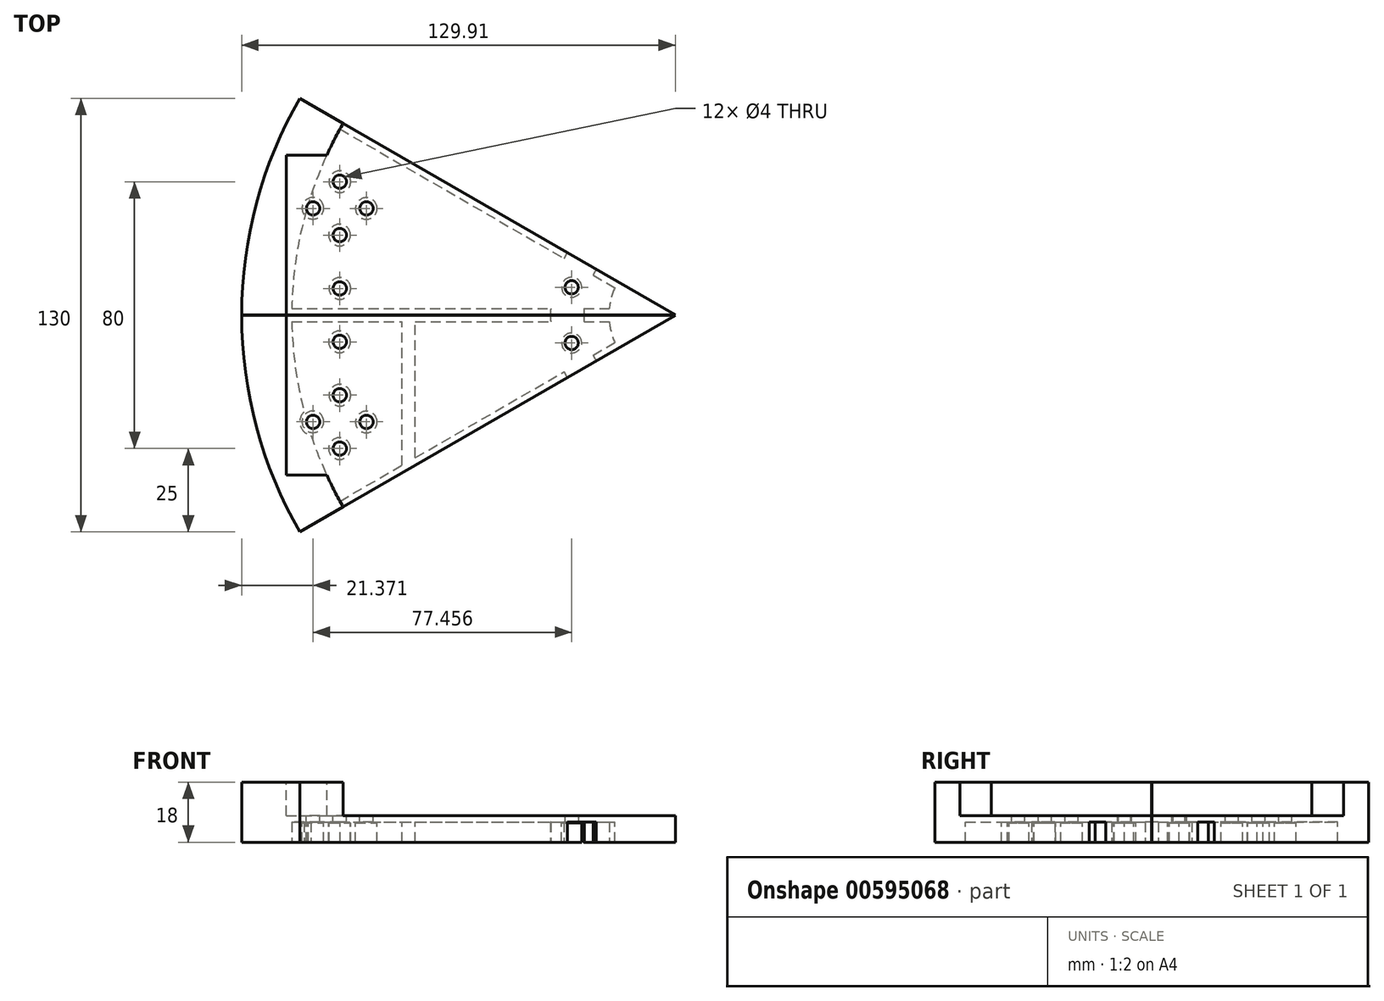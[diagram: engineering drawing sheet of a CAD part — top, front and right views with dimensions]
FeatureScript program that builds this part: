
annotation { "Feature Type Name" : "Feature", "Feature Type Description" : "" }
export const myFeature = defineFeature(function(context is Context, id is Id, definition is map)
    precondition{}
    {
        {
            var Q0;
            Q0=qCreatedBy(makeId("Front.planeOp"),FACE);
            var sketch = newSketch(context, id + "F0", { "sketchPlane" : qUnion([Q0])});
            skLineSegment(sketch, "E0.bottom", {"start": v(-45.23, 10.4) * mm, "end": v(-30.23, 10.4) * mm});
            skLineSegment(sketch, "E0.top", {"start": v(-45.23, -7.6) * mm, "end": v(-30.23, -7.6) * mm});
            skLineSegment(sketch, "E0.left", {"start": v(-45.23, 10.4) * mm, "end": v(-45.23, -7.6) * mm});
            skLineSegment(sketch, "E0.right", {"start": v(-30.23, 10.4) * mm, "end": v(-30.23, -7.6) * mm});
            skLineSegment(sketch, "E1.bottom", {"start": v(-30.23, -1.6) * mm, "end": v(84.77, -1.6) * mm});
            skLineSegment(sketch, "E1.top", {"start": v(-30.23, 0.4) * mm, "end": v(84.77, 0.4) * mm});
            skLineSegment(sketch, "E1.left", {"start": v(-30.23, -1.6) * mm, "end": v(-30.23, 0.4) * mm});
            skLineSegment(sketch, "E1.right", {"start": v(84.77, -1.6) * mm, "end": v(84.77, 0.4) * mm});
            skLineSegment(sketch, "E2.bottom", {"start": v(84.77, 0.4) * mm, "end": v(64.77, 0.4) * mm});
            skLineSegment(sketch, "E2.top", {"start": v(84.77, -7.6) * mm, "end": v(64.77, -7.6) * mm});
            skLineSegment(sketch, "E2.left", {"start": v(84.77, 0.4) * mm, "end": v(84.77, -7.6) * mm});
            skLineSegment(sketch, "E2.right", {"start": v(64.77, 0.4) * mm, "end": v(64.77, -7.6) * mm});
            skSolve(sketch);
        }
        {
            var Q0;
            {var subQ1=sQuery(id+"F0.wireOp",EDGE,"E0.bottom");Q0=makeQuery(id+"F0.imprint","IMPRINT",FACE,{"disambiguationData":[TD([[makeQuery(id+"F0.imprint","IMPRINT",EDGE,{"derivedFrom":subQ1}),-1.0]])]});}
            var Q1;
            {var subQ5=sQuery(id+"F0.wireOp",EDGE,"E2.top");Q1=makeQuery(id+"F0.imprint","IMPRINT",FACE,{"disambiguationData":[TD([[makeQuery(id+"F0.imprint","IMPRINT",EDGE,{"derivedFrom":subQ5}),-1.0]])]});}
            var Q2;
            {var subQ4=sQuery(id+"F0.wireOp",EDGE,"E1.top");Q2=makeQuery(id+"F0.imprint","IMPRINT",FACE,{"disambiguationData":[TD([[makeQuery(id+"F0.imprint","IMPRINT",EDGE,{"derivedFrom":subQ4}),-1.0]])]});}
            var Q3;
            {var subQ5=sQuery(id+"F0.wireOp",EDGE,"E2.bottom");Q3=makeQuery(id+"F0.imprint","IMPRINT",FACE,{"disambiguationData":[TD([[makeQuery(id+"F0.imprint","IMPRINT",EDGE,{"derivedFrom":subQ5}),1.0]])]});}
            var Q4;
            Q4=sQuery(id+"F0.wireOp",EDGE,"E1.right");
            revolve(context, id + "F1", {"entities" : qUnion([Q0, Q1, Q2, Q3]), "axis" : qUnion([Q4]), "revolveType" : RevolveType.SYMMETRIC, "angle" : 60 * degree});
        }
        {
            var Q0;
            Q0=makeQuery(id+"F1.opRevolve","SWEPT_FACE",FACE,{"disambiguationData":[OSD([sQuery(id+"F0.wireOp",EDGE,"E0.bottom")])]});
            var sketch = newSketch(context, id + "F2", { "sketchPlane" : qUnion([Q0])});
            skLineSegment(sketch, "E3.bottom", {"start": v(-31.86, 48) * mm, "end": v(0.14, 48) * mm});
            skLineSegment(sketch, "E3.top", {"start": v(-31.86, -48) * mm, "end": v(0.14, -48) * mm});
            skLineSegment(sketch, "E3.left", {"start": v(-31.86, 48) * mm, "end": v(-31.86, -48) * mm});
            skLineSegment(sketch, "E3.right", {"start": v(0.14, 48) * mm, "end": v(0.14, -48) * mm});
            skLineSegment(sketch, "E4", {"start": v(12.42, 124.7) * mm, "end": v(-58.42, 2) * mm});
            skSolve(sketch);
        }
        {
            var Q0;
            {var subQ0=sQuery(id+"F0.wireOp",EDGE,"E1.bottom");Q0=makeQuery(id+"F8.boolean.opBoolean","MERGE",FACE,{"derivedFrom":[makeQuery(id+"F1.opRevolve","SWEPT_FACE",FACE,{"disambiguationData":[OSD([subQ0])]}),makeQuery(id+"F8.opExtrude","CAP_FACE",FACE,{"disambiguationData":[OSD([subQ0]),OD(0.0)],"isStart":false}),makeQuery(id+"F8.opExtrude","CAP_FACE",FACE,{"disambiguationData":[OSD([subQ0]),OD(1.0)],"isStart":false})]});}
            var sketch = newSketch(context, id + "F3", { "sketchPlane" : qUnion([Q0])});
            skLineSegment(sketch, "E5.bottom", {"start": v(-42.98, 2) * mm, "end": v(77.02, 2) * mm});
            skLineSegment(sketch, "E5.top", {"start": v(-42.98, -2) * mm, "end": v(77.02, -2) * mm});
            skLineSegment(sketch, "E5.left", {"start": v(-42.98, 2) * mm, "end": v(-42.98, -2) * mm});
            skLineSegment(sketch, "E5.right", {"start": v(77.02, 2) * mm, "end": v(77.02, -2) * mm});
            skLineSegment(sketch, "E6.1.0", {"start": v(-26.87, -62.14) * mm, "end": v(77.06, -2.14) * mm});
            skLineSegment(sketch, "E6.1.1", {"start": v(-24.87, -65.6) * mm, "end": v(79.06, -5.6) * mm});
            skLineSegment(sketch, "E6.1.2", {"start": v(77.06, -2.14) * mm, "end": v(79.06, -5.6) * mm});
            skLineSegment(sketch, "E6.1.3", {"start": v(-26.87, -62.14) * mm, "end": v(-24.87, -65.6) * mm});
            skLineSegment(sketch, "E6.2.2", {"start": v(79.16, -5.71) * mm, "end": v(82.62, -7.71) * mm});
            skLineSegment(sketch, "E6.3.2", {"start": v(82.77, -7.75) * mm, "end": v(86.77, -7.75) * mm});
            skLineSegment(sketch, "E6.4.2", {"start": v(86.9, -7.71) * mm, "end": v(90.37, -5.71) * mm});
            skLineSegment(sketch, "E6.5.2", {"start": v(90.48, -5.6) * mm, "end": v(92.48, -2.14) * mm});
            skLineSegment(sketch, "E6.6.2", {"start": v(92.51, -2) * mm, "end": v(92.51, 2) * mm});
            skLineSegment(sketch, "E6.7.2", {"start": v(92.48, 2.14) * mm, "end": v(90.48, 5.6) * mm});
            skLineSegment(sketch, "E6.8.2", {"start": v(90.37, 5.71) * mm, "end": v(86.9, 7.71) * mm});
            skLineSegment(sketch, "E6.9.2", {"start": v(86.77, 7.75) * mm, "end": v(82.77, 7.75) * mm});
            skLineSegment(sketch, "E6.10.2", {"start": v(82.62, 7.71) * mm, "end": v(79.16, 5.71) * mm});
            skLineSegment(sketch, "E6.11.0", {"start": v(-24.87, 65.6) * mm, "end": v(79.06, 5.6) * mm});
            skLineSegment(sketch, "E6.11.1", {"start": v(-26.87, 62.14) * mm, "end": v(77.06, 2.14) * mm});
            skLineSegment(sketch, "E6.11.2", {"start": v(79.06, 5.6) * mm, "end": v(77.06, 2.14) * mm});
            skLineSegment(sketch, "E6.11.3", {"start": v(-24.87, 65.6) * mm, "end": v(-26.87, 62.14) * mm});
            skPoint(sketch, "E6.center", {"position": v(84.77, 0) * mm});
            skSolve(sketch);
        }
        {
            var Q0;
            {var subQ2=sQuery(id+"F0.wireOp",EDGE,"E1.bottom");var subQ10=makeQuery(id+"F1.opRevolve","CAP_EDGE",EDGE,{"disambiguationData":[OSD([subQ2])],"isStart":false});Q0=makeQuery(id+"F3.imprint","IMPRINT",FACE,{"disambiguationData":[TD([[makeQuery(id+"F3.imprint","IMPRINT",EDGE,{"derivedFrom":subQ10}),-1.0]])]});}
            var Q1;
            {var subQ0=sQuery(id+"F3.wireOp",EDGE,"E5.bottom");var subQ1=sQuery(id+"F0.wireOp",EDGE,"E1.bottom");var subQ2=makeQuery(id+"F1.opRevolve","SWEPT_EDGE",EDGE,{"disambiguationData":[OSD([subQ1,sQuery(id+"F0.wireOp",EDGE,"E2.right")])]});var subQ3=makeQuery(id+"F3.imprint","INTERSECT",VERTEX,{"derivedFrom":[subQ2,subQ0]});Q1=makeQuery(id+"F3.imprint","IMPRINT",FACE,{"disambiguationData":[TD([[makeQuery(id+"F3.imprint","IMPRINT",EDGE,{"disambiguationData":[TD([[subQ3,1.0]])],"derivedFrom":subQ0}),-1.0]])]});}
            var Q2;
            {var subQ2=sQuery(id+"F0.wireOp",EDGE,"E1.bottom");var subQ10=makeQuery(id+"F1.opRevolve","CAP_EDGE",EDGE,{"disambiguationData":[OSD([subQ2])],"isStart":true});Q2=makeQuery(id+"F3.imprint","IMPRINT",FACE,{"disambiguationData":[TD([[makeQuery(id+"F3.imprint","IMPRINT",EDGE,{"derivedFrom":subQ10}),1.0]])]});}
            var Q3;
            {var subQ0=sQuery(id+"F3.wireOp",EDGE,"E5.bottom");var subQ3=sQuery(id+"F0.wireOp",EDGE,"E1.bottom");var subQ4=makeQuery(id+"F1.opRevolve","SWEPT_FACE",FACE,{"disambiguationData":[OSD([subQ3])]});var subQ7=makeQuery(id+"F9.boolean.opBoolean","INTERSECT",EDGE,{"derivedFrom":[subQ4,makeQuery(id+"F9.opExtrude","SWEPT_FACE",FACE,{"disambiguationData":[OSD([sQuery(id+"F7.wireOp",EDGE,"E14.0.1.6")])]})]});var subQ8=makeQuery(id+"F3.imprint","INTERSECT",VERTEX,{"derivedFrom":[subQ7,subQ0]});Q3=makeQuery(id+"F3.imprint","IMPRINT",FACE,{"disambiguationData":[TD([[makeQuery(id+"F3.imprint","IMPRINT",EDGE,{"disambiguationData":[TD([[subQ8,1.0]])],"derivedFrom":subQ7}),1.0]])]});}
            var Q4;
            {var subQ0=sQuery(id+"F3.wireOp",EDGE,"E5.bottom");var subQ1=makeQuery(id+"F1.opRevolve","SWEPT_FACE",FACE,{"disambiguationData":[OSD([sQuery(id+"F0.wireOp",EDGE,"E1.bottom")])]});var subQ2=makeQuery(id+"F9.boolean.opBoolean","INTERSECT",EDGE,{"derivedFrom":[subQ1,makeQuery(id+"F9.opExtrude","SWEPT_FACE",FACE,{"disambiguationData":[OSD([sQuery(id+"F7.wireOp",EDGE,"E14.0.1.6")])]})]});var subQ3=makeQuery(id+"F3.imprint","INTERSECT",VERTEX,{"derivedFrom":[subQ2,subQ0]});Q4=makeQuery(id+"F3.imprint","IMPRINT",FACE,{"disambiguationData":[TD([[makeQuery(id+"F3.imprint","IMPRINT",EDGE,{"disambiguationData":[TD([[subQ3,-1.0]])],"derivedFrom":subQ0}),-1.0]])]});}
            extrude(context, id + "F4", {"entities" : qUnion([Q0, Q1, Q2, Q3, Q4]), "operationType" : NewBodyOperationType.ADD, "depth" : 6 * mm, "offsetDistance" : 25 * mm});
        }
        {
            var Q0;
            {var subQ0=sQuery(id+"F2.wireOp",EDGE,"E3.left");Q0=makeQuery(id+"F2.imprint","IMPRINT",FACE,{"disambiguationData":[TD([[makeQuery(id+"F2.imprint","IMPRINT",EDGE,{"derivedFrom":subQ0}),1.0]])]});}
            extrude(context, id + "F5", {"entities" : qUnion([Q0]), "operationType" : NewBodyOperationType.REMOVE, "oppositeDirection" : true, "depth" : 10 * mm, "offsetDistance" : 25 * mm});
        }
        {
            var Q0;
            {var subQ0=sQuery(id+"F0.wireOp",EDGE,"E2.right");var subQ1=sQuery(id+"F0.wireOp",EDGE,"E1.left");var subQ2=sQuery(id+"F0.wireOp",EDGE,"E1.bottom");var subQ3=sQuery(id+"F0.wireOp",EDGE,"E0.right");Q0=makeQuery(id+"F4.boolean.opBoolean","MERGE",FACE,{"derivedFrom":[makeQuery(id+"F1.opRevolve","SWEPT_FACE",FACE,{"disambiguationData":[OSD([sQuery(id+"F0.wireOp",EDGE,"E0.top")])]}),makeQuery(id+"F1.opRevolve","SWEPT_FACE",FACE,{"disambiguationData":[OSD([sQuery(id+"F0.wireOp",EDGE,"E2.top")])]}),makeQuery(id+"F4.opExtrude","CAP_FACE",FACE,{"disambiguationData":[OSD([sQuery(id+"F3.wireOp",EDGE,"E5.bottom"),sQuery(id+"F3.wireOp",EDGE,"E5.top"),sQuery(id+"F3.wireOp",EDGE,"E5.left"),sQuery(id+"F3.wireOp",EDGE,"E5.right")])],"isStart":false}),makeQuery(id+"F4.opExtrude","CAP_FACE",FACE,{"disambiguationData":[OSD([subQ3,subQ2,subQ1,subQ0,sQuery(id+"F3.wireOp",EDGE,"E6.1.0")])],"isStart":false}),makeQuery(id+"F4.opExtrude","CAP_FACE",FACE,{"disambiguationData":[OSD([subQ3,subQ2,subQ1,subQ0,sQuery(id+"F3.wireOp",EDGE,"E6.11.1")])],"isStart":false})]});}
            var sketch = newSketch(context, id + "F6", { "sketchPlane" : qUnion([Q0])});
            skCircle(sketch, "E7", {"center": v(-23.86, 32) * mm, "radius": 4 * mm});
            skCircle(sketch, "E8", {"center": v(-23.86, -32) * mm, "radius": 4 * mm});
            skCircle(sketch, "E9", {"center": v(-23.84, 0) * mm, "radius": 4 * mm});
            skCircle(sketch, "E10", {"center": v(-7.64, 0) * mm, "radius": 4 * mm});
            skSolve(sketch);
        }
        {
            var Q0;
            Q0=makeQuery(id+"F5.boolean.opBoolean","MERGE",FACE,{"derivedFrom":[makeQuery(id+"F1.opRevolve","SWEPT_FACE",FACE,{"disambiguationData":[OSD([sQuery(id+"F0.wireOp",EDGE,"E1.top"),sQuery(id+"F0.wireOp",EDGE,"E2.bottom")])]}),makeQuery(id+"F5.opExtrude","CAP_FACE",FACE,{"disambiguationData":[OSD([sQuery(id+"F0.wireOp",EDGE,"E0.bottom"),sQuery(id+"F0.wireOp",EDGE,"E0.right"),sQuery(id+"F2.wireOp",EDGE,"E3.bottom"),sQuery(id+"F2.wireOp",EDGE,"E3.top"),sQuery(id+"F2.wireOp",EDGE,"E3.left")])],"isStart":false})]});
            var sketch = newSketch(context, id + "F7", { "sketchPlane" : qUnion([Q0])});
            skCircle(sketch, "E11", {"center": v(-15.86, 32) * mm, "radius": 8 * mm});
            skCircle(sketch, "E12", {"center": v(-15.86, 40) * mm, "radius": 2 * mm});
            skCircle(sketch, "E13.1.0", {"center": v(-21.52, 37.66) * mm, "radius": 2 * mm});
            skCircle(sketch, "E13.2.0", {"center": v(-23.86, 32) * mm, "radius": 2 * mm});
            skCircle(sketch, "E13.3.0", {"center": v(-21.52, 26.34) * mm, "radius": 2 * mm});
            skCircle(sketch, "E13.4.0", {"center": v(-15.86, 24) * mm, "radius": 2 * mm});
            skCircle(sketch, "E13.5.0", {"center": v(-10.2, 26.34) * mm, "radius": 2 * mm});
            skCircle(sketch, "E13.6.0", {"center": v(-7.86, 32) * mm, "radius": 2 * mm});
            skCircle(sketch, "E13.7.0", {"center": v(-10.2, 37.66) * mm, "radius": 2 * mm});
            skCircle(sketch, "E14.0.1.0", {"center": v(-15.86, 8) * mm, "radius": 2 * mm});
            skCircle(sketch, "E14.0.1.1", {"center": v(-10.2, 5.66) * mm, "radius": 2 * mm});
            skCircle(sketch, "E14.0.1.2", {"center": v(-7.86, 0) * mm, "radius": 2 * mm});
            skCircle(sketch, "E14.0.1.3", {"center": v(-10.2, -5.66) * mm, "radius": 2 * mm});
            skCircle(sketch, "E14.0.1.4", {"center": v(-15.86, -8) * mm, "radius": 2 * mm});
            skCircle(sketch, "E14.0.1.5", {"center": v(-21.52, -5.66) * mm, "radius": 2 * mm});
            skCircle(sketch, "E14.0.1.6", {"center": v(-23.86, 0) * mm, "radius": 2 * mm});
            skCircle(sketch, "E14.0.1.7", {"center": v(-21.52, 5.66) * mm, "radius": 2 * mm});
            skCircle(sketch, "E14.0.2.0", {"center": v(-15.86, -24) * mm, "radius": 2 * mm});
            skCircle(sketch, "E14.0.2.1", {"center": v(-10.2, -26.34) * mm, "radius": 2 * mm});
            skCircle(sketch, "E14.0.2.2", {"center": v(-7.86, -32) * mm, "radius": 2 * mm});
            skCircle(sketch, "E14.0.2.3", {"center": v(-10.2, -37.66) * mm, "radius": 2 * mm});
            skCircle(sketch, "E14.0.2.4", {"center": v(-15.86, -40) * mm, "radius": 2 * mm});
            skCircle(sketch, "E14.0.2.5", {"center": v(-21.52, -37.66) * mm, "radius": 2 * mm});
            skCircle(sketch, "E14.0.2.6", {"center": v(-23.86, -32) * mm, "radius": 2 * mm});
            skCircle(sketch, "E14.0.2.7", {"center": v(-21.52, -26.34) * mm, "radius": 2 * mm});
            skLineSegment(sketch, "E14.direction1", {"start": v(-21.52, 26.34) * mm, "end": v(3.48, 26.34) * mm, "construction": true});
            skLineSegment(sketch, "E14.direction2", {"start": v(-21.52, 26.34) * mm, "end": v(-21.52, -5.66) * mm, "construction": true});
            skSolve(sketch);
        }
        {
            var Q0;
            {var subQ3=sQuery(id+"F0.wireOp",EDGE,"E0.top");var subQ5=makeQuery(id+"F1.opRevolve","SWEPT_FACE",FACE,{"disambiguationData":[OSD([subQ3])]});var subQ6=makeQuery(id+"F9.opExtrude","SWEPT_FACE",FACE,{"disambiguationData":[OSD([sQuery(id+"F7.wireOp",EDGE,"E13.2.0")])]});var subQ12=makeQuery(id+"F9.boolean.opBoolean","INTERSECT",EDGE,{"derivedFrom":[subQ5,subQ6]});Q0=makeQuery(id+"F6.imprint","IMPRINT",FACE,{"disambiguationData":[TD([[makeQuery(id+"F6.imprint","IMPRINT",EDGE,{"derivedFrom":subQ12}),1.0]])]});}
            var Q1;
            {var subQ3=sQuery(id+"F0.wireOp",EDGE,"E0.top");var subQ4=makeQuery(id+"F1.opRevolve","SWEPT_FACE",FACE,{"disambiguationData":[OSD([subQ3])]});var subQ6=makeQuery(id+"F9.opExtrude","SWEPT_FACE",FACE,{"disambiguationData":[OSD([sQuery(id+"F7.wireOp",EDGE,"E14.0.2.6")])]});var subQ12=makeQuery(id+"F9.boolean.opBoolean","INTERSECT",EDGE,{"derivedFrom":[subQ4,subQ6]});Q1=makeQuery(id+"F6.imprint","IMPRINT",FACE,{"disambiguationData":[TD([[makeQuery(id+"F6.imprint","IMPRINT",EDGE,{"derivedFrom":subQ12}),1.0]])]});}
            var Q2;
            {var subQ0=sQuery(id+"F6.wireOp",EDGE,"E9");var subQ1=makeQuery(id+"F4.opExtrude","CAP_EDGE",EDGE,{"disambiguationData":[OSD([sQuery(id+"F3.wireOp",EDGE,"E5.bottom")])],"isStart":false});var subQ2=makeQuery(id+"F6.imprint","INTERSECT",VERTEX,{"disambiguationData":[OD(0.0)],"derivedFrom":[subQ1,subQ0]});Q2=makeQuery(id+"F6.imprint","IMPRINT",FACE,{"disambiguationData":[TD([[makeQuery(id+"F6.imprint","IMPRINT",EDGE,{"disambiguationData":[TD([[subQ2,-1.0]])],"derivedFrom":subQ0}),1.0]])]});}
            var Q3;
            {var subQ0=sQuery(id+"F6.wireOp",EDGE,"E10");var subQ1=makeQuery(id+"F4.opExtrude","CAP_EDGE",EDGE,{"disambiguationData":[OSD([sQuery(id+"F3.wireOp",EDGE,"E5.bottom")])],"isStart":false});var subQ2=makeQuery(id+"F6.imprint","INTERSECT",VERTEX,{"disambiguationData":[OD(0.0)],"derivedFrom":[subQ1,subQ0]});Q3=makeQuery(id+"F6.imprint","IMPRINT",FACE,{"disambiguationData":[TD([[makeQuery(id+"F6.imprint","IMPRINT",EDGE,{"disambiguationData":[TD([[subQ2,-1.0]])],"derivedFrom":subQ0}),1.0]])]});}
            var Q4;
            {var subQ0=sQuery(id+"F6.wireOp",EDGE,"E7");var subQ1=sQuery(id+"F3.wireOp",EDGE,"E5.bottom");var subQ6=sQuery(id+"F0.wireOp",EDGE,"E0.right");var subQ7=sQuery(id+"F0.wireOp",EDGE,"E0.top");var subQ8=makeQuery(id+"F4.boolean.opBoolean","SPLIT",EDGE,{"disambiguationData":[TD([makeQuery(id+"F4.opExtrude","SWEPT_FACE",FACE,{"disambiguationData":[OSD([subQ1])]})])],"derivedFrom":makeQuery(id+"F1.opRevolve","SWEPT_EDGE",EDGE,{"disambiguationData":[OSD([subQ7,subQ6])]})});var subQ9=makeQuery(id+"F6.imprint","INTERSECT",VERTEX,{"disambiguationData":[OD(0.0)],"derivedFrom":[subQ8,subQ0]});Q4=makeQuery(id+"F6.imprint","IMPRINT",FACE,{"disambiguationData":[TD([[makeQuery(id+"F6.imprint","IMPRINT",EDGE,{"disambiguationData":[TD([[subQ9,-1.0]])],"derivedFrom":subQ0}),1.0]])]});}
            var Q5;
            {var subQ0=sQuery(id+"F6.wireOp",EDGE,"E8");var subQ1=sQuery(id+"F3.wireOp",EDGE,"E5.top");var subQ5=sQuery(id+"F0.wireOp",EDGE,"E0.right");var subQ6=sQuery(id+"F0.wireOp",EDGE,"E0.top");var subQ8=makeQuery(id+"F4.boolean.opBoolean","SPLIT",EDGE,{"disambiguationData":[TD([makeQuery(id+"F4.opExtrude","SWEPT_FACE",FACE,{"disambiguationData":[OSD([subQ1])]})])],"derivedFrom":makeQuery(id+"F1.opRevolve","SWEPT_EDGE",EDGE,{"disambiguationData":[OSD([subQ6,subQ5])]})});var subQ9=makeQuery(id+"F6.imprint","INTERSECT",VERTEX,{"disambiguationData":[OD(0.0)],"derivedFrom":[subQ8,subQ0]});Q5=makeQuery(id+"F6.imprint","IMPRINT",FACE,{"disambiguationData":[TD([[makeQuery(id+"F6.imprint","IMPRINT",EDGE,{"disambiguationData":[TD([[subQ9,1.0]])],"derivedFrom":subQ0}),1.0]])]});}
            var Q6;
            Q6=makeQuery(id+"F1.opRevolve","SWEPT_FACE",FACE,{"disambiguationData":[OSD([sQuery(id+"F0.wireOp",EDGE,"E1.bottom")])]});
            extrude(context, id + "F8", {"entities" : qUnion([Q0, Q1, Q2, Q3, Q4, Q5]), "operationType" : NewBodyOperationType.REMOVE, "endBound" : BoundingType.UP_TO_SURFACE, "oppositeDirection" : true, "depth" : 25 * mm, "endBoundEntityFace" : qUnion([Q6]), "offsetDistance" : 25 * mm});
        }
        {
            var Q0;
            Q0=makeQuery(id+"F7.imprint","IMPRINT",FACE,{"disambiguationData":[TD([[makeQuery(id+"F7.imprint","IMPRINT",EDGE,{"derivedFrom":sQuery(id+"F7.wireOp",EDGE,"E14.0.2.6")}),1.0]])]});
            var Q1;
            Q1=makeQuery(id+"F7.imprint","IMPRINT",FACE,{"disambiguationData":[TD([[makeQuery(id+"F7.imprint","IMPRINT",EDGE,{"derivedFrom":sQuery(id+"F7.wireOp",EDGE,"E14.0.2.4")}),1.0]])]});
            var Q2;
            Q2=makeQuery(id+"F7.imprint","IMPRINT",FACE,{"disambiguationData":[TD([[makeQuery(id+"F7.imprint","IMPRINT",EDGE,{"derivedFrom":sQuery(id+"F7.wireOp",EDGE,"E14.0.2.0")}),1.0]])]});
            var Q3;
            Q3=makeQuery(id+"F7.imprint","IMPRINT",FACE,{"disambiguationData":[TD([[makeQuery(id+"F7.imprint","IMPRINT",EDGE,{"derivedFrom":sQuery(id+"F7.wireOp",EDGE,"E14.0.2.2")}),1.0]])]});
            var Q4;
            Q4=makeQuery(id+"F7.imprint","IMPRINT",FACE,{"disambiguationData":[TD([[makeQuery(id+"F7.imprint","IMPRINT",EDGE,{"derivedFrom":sQuery(id+"F7.wireOp",EDGE,"E14.0.1.0")}),1.0]])]});
            var Q5;
            Q5=makeQuery(id+"F7.imprint","IMPRINT",FACE,{"disambiguationData":[TD([[makeQuery(id+"F7.imprint","IMPRINT",EDGE,{"derivedFrom":sQuery(id+"F7.wireOp",EDGE,"E14.0.1.4")}),1.0]])]});
            var Q6;
            {var subQ0=sQuery(id+"F7.wireOp",EDGE,"E12");var subQ1=sQuery(id+"F7.wireOp",EDGE,"E11");var subQ2=makeQuery(id+"F7.imprint","INTERSECT",VERTEX,{"disambiguationData":[OD(0.0)],"derivedFrom":[subQ1,subQ0]});Q6=makeQuery(id+"F7.imprint","IMPRINT",FACE,{"disambiguationData":[TD([[makeQuery(id+"F7.imprint","IMPRINT",EDGE,{"disambiguationData":[TD([[subQ2,-1.0]])],"derivedFrom":subQ1}),-1.0]])]});}
            var Q7;
            {var subQ0=sQuery(id+"F7.wireOp",EDGE,"E12");var subQ1=sQuery(id+"F7.wireOp",EDGE,"E11");var subQ2=makeQuery(id+"F7.imprint","INTERSECT",VERTEX,{"disambiguationData":[OD(0.0)],"derivedFrom":[subQ1,subQ0]});Q7=makeQuery(id+"F7.imprint","IMPRINT",FACE,{"disambiguationData":[TD([[makeQuery(id+"F7.imprint","IMPRINT",EDGE,{"disambiguationData":[TD([[subQ2,-1.0]])],"derivedFrom":subQ1}),1.0]])]});}
            var Q8;
            {var subQ0=sQuery(id+"F7.wireOp",EDGE,"E13.2.0");var subQ1=sQuery(id+"F7.wireOp",EDGE,"E11");var subQ2=makeQuery(id+"F7.imprint","INTERSECT",VERTEX,{"disambiguationData":[OD(0.0)],"derivedFrom":[subQ1,subQ0]});Q8=makeQuery(id+"F7.imprint","IMPRINT",FACE,{"disambiguationData":[TD([[makeQuery(id+"F7.imprint","IMPRINT",EDGE,{"disambiguationData":[TD([[subQ2,-1.0]])],"derivedFrom":subQ1}),1.0]])]});}
            var Q9;
            {var subQ0=sQuery(id+"F7.wireOp",EDGE,"E13.4.0");var subQ1=sQuery(id+"F7.wireOp",EDGE,"E11");var subQ2=makeQuery(id+"F7.imprint","INTERSECT",VERTEX,{"disambiguationData":[OD(0.0)],"derivedFrom":[subQ1,subQ0]});Q9=makeQuery(id+"F7.imprint","IMPRINT",FACE,{"disambiguationData":[TD([[makeQuery(id+"F7.imprint","IMPRINT",EDGE,{"disambiguationData":[TD([[subQ2,-1.0]])],"derivedFrom":subQ1}),-1.0]])]});}
            var Q10;
            {var subQ0=sQuery(id+"F7.wireOp",EDGE,"E13.4.0");var subQ1=sQuery(id+"F7.wireOp",EDGE,"E11");var subQ2=makeQuery(id+"F7.imprint","INTERSECT",VERTEX,{"disambiguationData":[OD(0.0)],"derivedFrom":[subQ1,subQ0]});Q10=makeQuery(id+"F7.imprint","IMPRINT",FACE,{"disambiguationData":[TD([[makeQuery(id+"F7.imprint","IMPRINT",EDGE,{"disambiguationData":[TD([[subQ2,-1.0]])],"derivedFrom":subQ1}),1.0]])]});}
            var Q11;
            {var subQ0=sQuery(id+"F7.wireOp",EDGE,"E13.2.0");var subQ1=sQuery(id+"F7.wireOp",EDGE,"E11");var subQ2=makeQuery(id+"F7.imprint","INTERSECT",VERTEX,{"disambiguationData":[OD(0.0)],"derivedFrom":[subQ1,subQ0]});Q11=makeQuery(id+"F7.imprint","IMPRINT",FACE,{"disambiguationData":[TD([[makeQuery(id+"F7.imprint","IMPRINT",EDGE,{"disambiguationData":[TD([[subQ2,-1.0]])],"derivedFrom":subQ1}),-1.0]])]});}
            var Q12;
            {var subQ0=sQuery(id+"F7.wireOp",EDGE,"E13.6.0");var subQ1=sQuery(id+"F7.wireOp",EDGE,"E11");var subQ2=makeQuery(id+"F7.imprint","INTERSECT",VERTEX,{"disambiguationData":[OD(0.0)],"derivedFrom":[subQ1,subQ0]});Q12=makeQuery(id+"F7.imprint","IMPRINT",FACE,{"disambiguationData":[TD([[makeQuery(id+"F7.imprint","IMPRINT",EDGE,{"disambiguationData":[TD([[subQ2,1.0]])],"derivedFrom":subQ1}),1.0]])]});}
            var Q13;
            {var subQ0=sQuery(id+"F7.wireOp",EDGE,"E13.6.0");var subQ1=sQuery(id+"F7.wireOp",EDGE,"E11");var subQ2=makeQuery(id+"F7.imprint","INTERSECT",VERTEX,{"disambiguationData":[OD(0.0)],"derivedFrom":[subQ1,subQ0]});Q13=makeQuery(id+"F7.imprint","IMPRINT",FACE,{"disambiguationData":[TD([[makeQuery(id+"F7.imprint","IMPRINT",EDGE,{"disambiguationData":[TD([[subQ2,1.0]])],"derivedFrom":subQ1}),-1.0]])]});}
            extrude(context, id + "F9", {"entities" : qUnion([Q0, Q1, Q2, Q3, Q4, Q5, Q6, Q7, Q8, Q9, Q10, Q11, Q12, Q13]), "operationType" : NewBodyOperationType.REMOVE, "endBound" : BoundingType.THROUGH_ALL, "oppositeDirection" : true, "depth" : 25 * mm, "offsetDistance" : 25 * mm});
        }
        {
            var Q0;
            {var subQ0=sQuery(id+"F3.wireOp",EDGE,"E5.top");var subQ1=sQuery(id+"F3.wireOp",EDGE,"E5.bottom");var subQ2=sQuery(id+"F0.wireOp",EDGE,"E0.right");var subQ3=sQuery(id+"F0.wireOp",EDGE,"E0.top");var subQ4=sQuery(id+"F0.wireOp",EDGE,"E1.bottom");var subQ7=makeQuery(id+"F1.opRevolve","SWEPT_FACE",FACE,{"disambiguationData":[OSD([subQ4])]});Q0=makeQuery(id+"F8.boolean.opBoolean","MERGE",FACE,{"derivedFrom":[makeQuery(id+"F4.boolean.opBoolean","SPLIT",FACE,{"disambiguationData":[TD([makeQuery(id+"F4.opExtrude","SWEPT_FACE",FACE,{"disambiguationData":[OSD([subQ1])]})])],"derivedFrom":subQ7}),makeQuery(id+"F4.boolean.opBoolean","SPLIT",FACE,{"disambiguationData":[TD([makeQuery(id+"F4.opExtrude","SWEPT_FACE",FACE,{"disambiguationData":[OSD([subQ0])]})])],"derivedFrom":subQ7}),makeQuery(id+"F8.opExtrude","CAP_FACE",FACE,{"disambiguationData":[OSD([subQ3,subQ2,sQuery(id+"F6.wireOp",EDGE,"E7")])],"isStart":false}),makeQuery(id+"F8.opExtrude","CAP_FACE",FACE,{"disambiguationData":[OSD([subQ3,subQ2,sQuery(id+"F6.wireOp",EDGE,"E8")])],"isStart":false}),makeQuery(id+"F8.opExtrude","CAP_FACE",FACE,{"disambiguationData":[OSD([subQ1,subQ0,sQuery(id+"F6.wireOp",EDGE,"E9")])],"isStart":false}),makeQuery(id+"F8.opExtrude","CAP_FACE",FACE,{"disambiguationData":[OSD([subQ1,subQ0,sQuery(id+"F6.wireOp",EDGE,"E10")])],"isStart":false})]});}
            var sketch = newSketch(context, id + "F10", { "sketchPlane" : qUnion([Q0])});
            skLineSegment(sketch, "E15.bottom", {"start": v(2.77, 75) * mm, "end": v(6.77, 75) * mm});
            skLineSegment(sketch, "E15.top", {"start": v(2.77, -75) * mm, "end": v(6.77, -75) * mm});
            skLineSegment(sketch, "E15.left", {"start": v(2.77, 75) * mm, "end": v(2.77, -75) * mm});
            skLineSegment(sketch, "E15.right", {"start": v(6.77, 75) * mm, "end": v(6.77, -75) * mm});
            skSolve(sketch);
        }
        {
            var Q0;
            {var subQ0=sQuery(id+"F10.wireOp",EDGE,"E15.left");var subQ1=makeQuery(id+"F4.opExtrude","CAP_EDGE",EDGE,{"disambiguationData":[OSD([sQuery(id+"F3.wireOp",EDGE,"E6.1.0")])],"isStart":true});var subQ2=makeQuery(id+"F10.imprint","INTERSECT",VERTEX,{"derivedFrom":[subQ1,subQ0]});Q0=makeQuery(id+"F10.imprint","IMPRINT",FACE,{"disambiguationData":[TD([[makeQuery(id+"F10.imprint","IMPRINT",EDGE,{"disambiguationData":[TD([[subQ2,-1.0]])],"derivedFrom":subQ1}),1.0]])]});}
            var Q1;
            {var subQ0=sQuery(id+"F10.wireOp",EDGE,"E15.left");var subQ1=makeQuery(id+"F4.opExtrude","CAP_EDGE",EDGE,{"disambiguationData":[OSD([sQuery(id+"F3.wireOp",EDGE,"E6.11.1")])],"isStart":true});var subQ2=makeQuery(id+"F10.imprint","INTERSECT",VERTEX,{"derivedFrom":[subQ1,subQ0]});Q1=makeQuery(id+"F10.imprint","IMPRINT",FACE,{"disambiguationData":[TD([[makeQuery(id+"F10.imprint","IMPRINT",EDGE,{"disambiguationData":[TD([[subQ2,-1.0]])],"derivedFrom":subQ1}),-1.0]])]});}
            extrude(context, id + "F11", {"entities" : qUnion([Q0, Q1]), "operationType" : NewBodyOperationType.ADD, "depth" : 6 * mm, "offsetDistance" : 25 * mm});
        }
        {
            var Q0;
            {var subQ0=sQuery(id+"F10.wireOp",EDGE,"E15.right");var subQ1=sQuery(id+"F10.wireOp",EDGE,"E15.left");var subQ2=sQuery(id+"F3.wireOp",EDGE,"E6.1.0");var subQ3=sQuery(id+"F3.wireOp",EDGE,"E5.top");var subQ4=sQuery(id+"F3.wireOp",EDGE,"E6.11.1");var subQ5=sQuery(id+"F3.wireOp",EDGE,"E5.bottom");var subQ9=sQuery(id+"F0.wireOp",EDGE,"E1.bottom");var subQ10=sQuery(id+"F0.wireOp",EDGE,"E2.right");var subQ12=sQuery(id+"F0.wireOp",EDGE,"E2.top");var subQ15=sQuery(id+"F0.wireOp",EDGE,"E0.right");var subQ16=sQuery(id+"F0.wireOp",EDGE,"E0.left");var subQ17=sQuery(id+"F0.wireOp",EDGE,"E0.top");var subQ19=sQuery(id+"F0.wireOp",EDGE,"E1.left");Q0=makeQuery(id+"F11.boolean.opBoolean","MERGE",FACE,{"derivedFrom":[makeQuery(id+"F8.boolean.opBoolean","SPLIT",FACE,{"disambiguationData":[TD([makeQuery(id+"F1.opRevolve","SWEPT_FACE",FACE,{"disambiguationData":[OSD([subQ16])]})])],"derivedFrom":makeQuery(id+"F4.boolean.opBoolean","MERGE",FACE,{"derivedFrom":[makeQuery(id+"F1.opRevolve","SWEPT_FACE",FACE,{"disambiguationData":[OSD([subQ17])]}),makeQuery(id+"F1.opRevolve","SWEPT_FACE",FACE,{"disambiguationData":[OSD([subQ12])]}),makeQuery(id+"F4.opExtrude","CAP_FACE",FACE,{"disambiguationData":[OSD([subQ5,subQ3,sQuery(id+"F3.wireOp",EDGE,"E5.left"),sQuery(id+"F3.wireOp",EDGE,"E5.right")])],"isStart":false}),makeQuery(id+"F4.opExtrude","CAP_FACE",FACE,{"disambiguationData":[OSD([subQ15,subQ9,subQ19,subQ10,subQ2])],"isStart":false}),makeQuery(id+"F4.opExtrude","CAP_FACE",FACE,{"disambiguationData":[OSD([subQ15,subQ9,subQ19,subQ10,subQ4])],"isStart":false})]})}),makeQuery(id+"F11.opExtrude","CAP_FACE",FACE,{"disambiguationData":[OSD([subQ5,subQ4,subQ1,subQ0])],"isStart":false}),makeQuery(id+"F11.opExtrude","CAP_FACE",FACE,{"disambiguationData":[OSD([subQ3,subQ2,subQ1,subQ0])],"isStart":false})]});}
            var sketch = newSketch(context, id + "F12", { "sketchPlane" : qUnion([Q0])});
            skCircle(sketch, "E16", {"center": v(84.77, 0) * mm, "radius": 27.5 * mm});
            skCircle(sketch, "E17", {"center": v(84.77, 0) * mm, "radius": 37.5 * mm});
            skSolve(sketch);
        }
        {
            var Q0;
            {var subQ5=sQuery(id+"F0.wireOp",EDGE,"E2.top");var subQ8=sQuery(id+"F0.wireOp",EDGE,"E1.bottom");var subQ10=sQuery(id+"F0.wireOp",EDGE,"E0.top");var subQ17=makeQuery(id+"F4.boolean.opBoolean","MERGE",EDGE,{"derivedFrom":[makeQuery(id+"F1.opRevolve","CAP_EDGE",EDGE,{"disambiguationData":[OSD([subQ10])],"isStart":false}),makeQuery(id+"F1.opRevolve","CAP_EDGE",EDGE,{"disambiguationData":[OSD([subQ5])],"isStart":false}),makeQuery(id+"F4.opExtrude","CAP_EDGE",EDGE,{"disambiguationData":[OSD([subQ8]),TDD([makeQuery(id+"F3.imprint","IMPRINT",EDGE,{"derivedFrom":makeQuery(id+"F1.opRevolve","CAP_EDGE",EDGE,{"disambiguationData":[OSD([subQ8])],"isStart":false})})])],"isStart":false})]});var subQ19=sQuery(id+"F12.wireOp",EDGE,"E17");var subQ20=makeQuery(id+"F12.imprint","INTERSECT",VERTEX,{"derivedFrom":[subQ17,subQ19]});Q0=makeQuery(id+"F12.imprint","IMPRINT",FACE,{"disambiguationData":[TD([[makeQuery(id+"F12.imprint","IMPRINT",EDGE,{"disambiguationData":[TD([[subQ20,-1.0]])],"derivedFrom":subQ17}),-1.0]])]});}
            var Q1;
            {var subQ0=sQuery(id+"F12.wireOp",EDGE,"E16");var subQ1=sQuery(id+"F3.wireOp",EDGE,"E5.bottom");var subQ5=sQuery(id+"F0.wireOp",EDGE,"E2.right");var subQ10=makeQuery(id+"F1.opRevolve","SWEPT_FACE",FACE,{"disambiguationData":[OSD([subQ5])]});var subQ23=makeQuery(id+"F4.opExtrude","CAP_EDGE",EDGE,{"disambiguationData":[OSD([subQ1])],"isStart":false});var subQ30=makeQuery(id+"F11.boolean.opBoolean","SPLIT",EDGE,{"disambiguationData":[TD([subQ10])],"derivedFrom":makeQuery(id+"F8.boolean.opBoolean","SPLIT",EDGE,{"disambiguationData":[TD([subQ10])],"derivedFrom":subQ23})});var subQ31=makeQuery(id+"F12.imprint","INTERSECT",VERTEX,{"derivedFrom":[subQ30,subQ0]});Q1=makeQuery(id+"F12.imprint","IMPRINT",FACE,{"disambiguationData":[TD([[makeQuery(id+"F12.imprint","IMPRINT",EDGE,{"disambiguationData":[TD([[subQ31,-1.0]])],"derivedFrom":subQ0}),-1.0]])]});}
            var Q2;
            {var subQ5=sQuery(id+"F0.wireOp",EDGE,"E2.top");var subQ8=sQuery(id+"F0.wireOp",EDGE,"E1.bottom");var subQ10=sQuery(id+"F0.wireOp",EDGE,"E0.top");var subQ17=makeQuery(id+"F4.boolean.opBoolean","MERGE",EDGE,{"derivedFrom":[makeQuery(id+"F1.opRevolve","CAP_EDGE",EDGE,{"disambiguationData":[OSD([subQ10])],"isStart":true}),makeQuery(id+"F1.opRevolve","CAP_EDGE",EDGE,{"disambiguationData":[OSD([subQ5])],"isStart":true}),makeQuery(id+"F4.opExtrude","CAP_EDGE",EDGE,{"disambiguationData":[OSD([subQ8]),TDD([makeQuery(id+"F3.imprint","IMPRINT",EDGE,{"derivedFrom":makeQuery(id+"F1.opRevolve","CAP_EDGE",EDGE,{"disambiguationData":[OSD([subQ8])],"isStart":true})})])],"isStart":false})]});var subQ19=sQuery(id+"F12.wireOp",EDGE,"E17");var subQ20=makeQuery(id+"F12.imprint","INTERSECT",VERTEX,{"derivedFrom":[subQ17,subQ19]});Q2=makeQuery(id+"F12.imprint","IMPRINT",FACE,{"disambiguationData":[TD([[makeQuery(id+"F12.imprint","IMPRINT",EDGE,{"disambiguationData":[TD([[subQ20,-1.0]])],"derivedFrom":subQ17}),1.0]])]});}
            var Q3;
            {var subQ1=sQuery(id+"F3.wireOp",EDGE,"E5.bottom");var subQ2=makeQuery(id+"F4.opExtrude","SWEPT_FACE",FACE,{"disambiguationData":[OSD([subQ1])]});var subQ3=sQuery(id+"F10.wireOp",EDGE,"E15.right");var subQ4=sQuery(id+"F3.wireOp",EDGE,"E6.11.1");var subQ5=sQuery(id+"F0.wireOp",EDGE,"E0.right");var subQ6=sQuery(id+"F0.wireOp",EDGE,"E0.top");var subQ7=makeQuery(id+"F8.opExtrude","CAP_FACE",FACE,{"disambiguationData":[OSD([subQ6,subQ5,sQuery(id+"F6.wireOp",EDGE,"E7")])],"isStart":false});var subQ8=sQuery(id+"F6.wireOp",EDGE,"E10");var subQ9=sQuery(id+"F3.wireOp",EDGE,"E5.top");var subQ10=makeQuery(id+"F8.opExtrude","CAP_FACE",FACE,{"disambiguationData":[OSD([subQ1,subQ9,subQ8])],"isStart":false});var subQ11=sQuery(id+"F0.wireOp",EDGE,"E1.bottom");var subQ12=makeQuery(id+"F1.opRevolve","SWEPT_FACE",FACE,{"disambiguationData":[OSD([subQ11])]});var subQ13=makeQuery(id+"F8.opExtrude","CAP_FACE",FACE,{"disambiguationData":[OSD([subQ6,subQ5,sQuery(id+"F6.wireOp",EDGE,"E8")])],"isStart":false});var subQ14=makeQuery(id+"F8.opExtrude","CAP_FACE",FACE,{"disambiguationData":[OSD([subQ1,subQ9,sQuery(id+"F6.wireOp",EDGE,"E9")])],"isStart":false});Q3=makeQuery(id+"F11.boolean.opBoolean","SPLIT",FACE,{"disambiguationData":[TD([makeQuery(id+"F11.opExtrude","SWEPT_FACE",FACE,{"disambiguationData":[OSD([subQ3]),TDD([makeQuery(id+"F10.imprint","IMPRINT",EDGE,{"disambiguationData":[TD([[makeQuery(id+"F10.imprint","INTERSECT",VERTEX,{"derivedFrom":[makeQuery(id+"F4.opExtrude","CAP_EDGE",EDGE,{"disambiguationData":[OSD([subQ4])],"isStart":true}),subQ3]}),-1.0]])],"derivedFrom":subQ3})])]})])],"derivedFrom":makeQuery(id+"F8.boolean.opBoolean","MERGE",FACE,{"derivedFrom":[makeQuery(id+"F4.boolean.opBoolean","SPLIT",FACE,{"disambiguationData":[TD([subQ2])],"derivedFrom":subQ12}),makeQuery(id+"F4.boolean.opBoolean","SPLIT",FACE,{"disambiguationData":[TD([makeQuery(id+"F4.opExtrude","SWEPT_FACE",FACE,{"disambiguationData":[OSD([subQ9])]})])],"derivedFrom":subQ12}),subQ7,subQ13,subQ14,subQ10]})});}
            extrude(context, id + "F13", {"entities" : qUnion([Q0, Q1, Q2]), "operationType" : NewBodyOperationType.REMOVE, "endBound" : BoundingType.UP_TO_SURFACE, "oppositeDirection" : true, "depth" : 25 * mm, "endBoundEntityFace" : qUnion([Q3]), "offsetDistance" : 25 * mm});
        }
        {
            var Q0;
            {var subQ0=sQuery(id+"F12.wireOp",EDGE,"E17");var subQ1=sQuery(id+"F12.wireOp",EDGE,"E16");var subQ2=sQuery(id+"F3.wireOp",EDGE,"E6.1.0");var subQ3=sQuery(id+"F0.wireOp",EDGE,"E2.top");var subQ4=sQuery(id+"F0.wireOp",EDGE,"E1.bottom");var subQ5=sQuery(id+"F0.wireOp",EDGE,"E0.top");var subQ6=sQuery(id+"F3.wireOp",EDGE,"E5.top");var subQ7=sQuery(id+"F3.wireOp",EDGE,"E5.bottom");var subQ8=sQuery(id+"F3.wireOp",EDGE,"E6.11.1");var subQ10=makeQuery(id+"F4.opExtrude","SWEPT_FACE",FACE,{"disambiguationData":[OSD([subQ7])]});var subQ11=sQuery(id+"F10.wireOp",EDGE,"E15.right");var subQ12=sQuery(id+"F0.wireOp",EDGE,"E0.right");var subQ13=makeQuery(id+"F8.opExtrude","CAP_FACE",FACE,{"disambiguationData":[OSD([subQ5,subQ12,sQuery(id+"F6.wireOp",EDGE,"E7")])],"isStart":false});var subQ14=sQuery(id+"F6.wireOp",EDGE,"E10");var subQ16=makeQuery(id+"F8.opExtrude","CAP_FACE",FACE,{"disambiguationData":[OSD([subQ7,subQ6,subQ14])],"isStart":false});var subQ17=makeQuery(id+"F1.opRevolve","SWEPT_FACE",FACE,{"disambiguationData":[OSD([subQ4])]});var subQ18=makeQuery(id+"F8.opExtrude","CAP_FACE",FACE,{"disambiguationData":[OSD([subQ5,subQ12,sQuery(id+"F6.wireOp",EDGE,"E8")])],"isStart":false});var subQ19=makeQuery(id+"F8.opExtrude","CAP_FACE",FACE,{"disambiguationData":[OSD([subQ7,subQ6,sQuery(id+"F6.wireOp",EDGE,"E9")])],"isStart":false});var subQ23=makeQuery(id+"F4.opExtrude","SWEPT_FACE",FACE,{"disambiguationData":[OSD([subQ6])]});var subQ24=makeQuery(id+"F8.boolean.opBoolean","MERGE",FACE,{"derivedFrom":[makeQuery(id+"F4.boolean.opBoolean","SPLIT",FACE,{"disambiguationData":[TD([subQ10])],"derivedFrom":subQ17}),makeQuery(id+"F4.boolean.opBoolean","SPLIT",FACE,{"disambiguationData":[TD([subQ23])],"derivedFrom":subQ17}),subQ13,subQ18,subQ19,subQ16]});Q0=makeQuery(id+"F13.boolean.opBoolean","MERGE",FACE,{"derivedFrom":[makeQuery(id+"F11.boolean.opBoolean","SPLIT",FACE,{"disambiguationData":[TD([makeQuery(id+"F11.opExtrude","SWEPT_FACE",FACE,{"disambiguationData":[OSD([subQ11]),TDD([makeQuery(id+"F10.imprint","IMPRINT",EDGE,{"disambiguationData":[TD([[makeQuery(id+"F10.imprint","INTERSECT",VERTEX,{"derivedFrom":[makeQuery(id+"F4.opExtrude","CAP_EDGE",EDGE,{"disambiguationData":[OSD([subQ2])],"isStart":true}),subQ11]}),1.0]])],"derivedFrom":subQ11})])]})])],"derivedFrom":subQ24}),makeQuery(id+"F11.boolean.opBoolean","SPLIT",FACE,{"disambiguationData":[TD([makeQuery(id+"F11.opExtrude","SWEPT_FACE",FACE,{"disambiguationData":[OSD([subQ11]),TDD([makeQuery(id+"F10.imprint","IMPRINT",EDGE,{"disambiguationData":[TD([[makeQuery(id+"F10.imprint","INTERSECT",VERTEX,{"derivedFrom":[makeQuery(id+"F4.opExtrude","CAP_EDGE",EDGE,{"disambiguationData":[OSD([subQ8])],"isStart":true}),subQ11]}),-1.0]])],"derivedFrom":subQ11})])]})])],"derivedFrom":subQ24}),makeQuery(id+"F13.opExtrude","CAP_FACE",FACE,{"disambiguationData":[OSD([subQ5,subQ4,subQ3,subQ8,subQ1,subQ0])],"isStart":false}),makeQuery(id+"F13.opExtrude","CAP_FACE",FACE,{"disambiguationData":[OSD([subQ7,subQ6,subQ1,subQ0])],"isStart":false}),makeQuery(id+"F13.opExtrude","CAP_FACE",FACE,{"disambiguationData":[OSD([subQ5,subQ4,subQ3,subQ2,subQ1,subQ0])],"isStart":false})]});}
            var sketch = newSketch(context, id + "F14", { "sketchPlane" : qUnion([Q0])});
            skCircle(sketch, "E18", {"center": v(53.6, 8.35) * mm, "radius": 2 * mm});
            skCircle(sketch, "E19.1.0", {"center": v(53.6, -8.35) * mm, "radius": 2 * mm});
            skCircle(sketch, "E19.2.0", {"center": v(61.95, -22.82) * mm, "radius": 2 * mm});
            skCircle(sketch, "E19.3.0", {"center": v(76.41, -31.17) * mm, "radius": 2 * mm});
            skCircle(sketch, "E19.4.0", {"center": v(93.12, -31.17) * mm, "radius": 2 * mm});
            skCircle(sketch, "E19.5.0", {"center": v(107.58, -22.82) * mm, "radius": 2 * mm});
            skCircle(sketch, "E19.6.0", {"center": v(115.93, -8.35) * mm, "radius": 2 * mm});
            skCircle(sketch, "E19.7.0", {"center": v(115.93, 8.35) * mm, "radius": 2 * mm});
            skCircle(sketch, "E19.8.0", {"center": v(107.58, 22.82) * mm, "radius": 2 * mm});
            skCircle(sketch, "E19.9.0", {"center": v(93.12, 31.17) * mm, "radius": 2 * mm});
            skCircle(sketch, "E19.10.0", {"center": v(76.41, 31.17) * mm, "radius": 2 * mm});
            skCircle(sketch, "E19.11.0", {"center": v(61.95, 22.82) * mm, "radius": 2 * mm});
            skPoint(sketch, "E19.center", {"position": v(84.77, 0) * mm});
            skSolve(sketch);
        }
        {
            var Q0;
            Q0=makeQuery(id+"F14.imprint","IMPRINT",FACE,{"disambiguationData":[TD([[makeQuery(id+"F14.imprint","IMPRINT",EDGE,{"derivedFrom":sQuery(id+"F14.wireOp",EDGE,"E18")}),1.0]])]});
            var Q1;
            Q1=makeQuery(id+"F14.imprint","IMPRINT",FACE,{"disambiguationData":[TD([[makeQuery(id+"F14.imprint","IMPRINT",EDGE,{"derivedFrom":sQuery(id+"F14.wireOp",EDGE,"E19.1.0")}),1.0]])]});
            var Q2;
            Q2=sQuery(id+"F14.wireOp",EDGE,"E18");
            var Q3;
            Q3=sQuery(id+"F14.wireOp",EDGE,"E19.1.0");
            extrude(context, id + "F15", {"entities" : qUnion([Q0, Q1]), "operationType" : NewBodyOperationType.REMOVE, "surfaceEntities" : qUnion([Q2, Q3]), "endBound" : BoundingType.THROUGH_ALL, "oppositeDirection" : true, "depth" : 25 * mm, "offsetDistance" : 25 * mm});
        }
        {
            var Q0;
            {var subQ0=sQuery(id+"F6.wireOp",EDGE,"E10");var subQ1=sQuery(id+"F3.wireOp",EDGE,"E5.bottom");var subQ3=sQuery(id+"F3.wireOp",EDGE,"E5.top");var subQ6=sQuery(id+"F6.wireOp",EDGE,"E9");var subQ7=makeQuery(id+"F4.opExtrude","SWEPT_FACE",FACE,{"disambiguationData":[OSD([subQ3])]});var subQ8=makeQuery(id+"F4.opExtrude","SWEPT_FACE",FACE,{"disambiguationData":[OSD([subQ1])]});var subQ11=sQuery(id+"F0.wireOp",EDGE,"E0.right");var subQ12=sQuery(id+"F0.wireOp",EDGE,"E0.top");var subQ13=sQuery(id+"F0.wireOp",EDGE,"E1.bottom");var subQ17=sQuery(id+"F6.wireOp",EDGE,"E7");var subQ18=sQuery(id+"F6.wireOp",EDGE,"E8");var subQ20=makeQuery(id+"F8.opExtrude","CAP_FACE",FACE,{"disambiguationData":[OSD([subQ12,subQ11,subQ17])],"isStart":false});var subQ22=makeQuery(id+"F8.opExtrude","CAP_FACE",FACE,{"disambiguationData":[OSD([subQ1,subQ3,subQ0])],"isStart":false});var subQ23=makeQuery(id+"F1.opRevolve","SWEPT_FACE",FACE,{"disambiguationData":[OSD([subQ13])]});var subQ24=makeQuery(id+"F8.opExtrude","CAP_FACE",FACE,{"disambiguationData":[OSD([subQ12,subQ11,subQ18])],"isStart":false});var subQ25=makeQuery(id+"F8.opExtrude","CAP_FACE",FACE,{"disambiguationData":[OSD([subQ1,subQ3,subQ6])],"isStart":false});Q0=makeQuery(id+"F11.boolean.opBoolean","SPLIT",FACE,{"disambiguationData":[TD([makeQuery(id+"F8.boolean.opBoolean","COPY",FACE,{"derivedFrom":makeQuery(id+"F8.opExtrude","SWEPT_FACE",FACE,{"disambiguationData":[OSD([subQ17])]})})])],"derivedFrom":makeQuery(id+"F8.boolean.opBoolean","MERGE",FACE,{"derivedFrom":[makeQuery(id+"F4.boolean.opBoolean","SPLIT",FACE,{"disambiguationData":[TD([subQ8])],"derivedFrom":subQ23}),makeQuery(id+"F4.boolean.opBoolean","SPLIT",FACE,{"disambiguationData":[TD([subQ7])],"derivedFrom":subQ23}),subQ20,subQ24,subQ25,subQ22]})});}
            var sketch = newSketch(context, id + "F16", { "sketchPlane" : qUnion([Q0])});
            skCircle(sketch, "E20", {"center": v(-15.86, -40) * mm, "radius": 3.25 * mm});
            skCircle(sketch, "E21.1.0", {"center": v(-7.9, -31.96) * mm, "radius": 3.25 * mm});
            skCircle(sketch, "E21.2.0", {"center": v(-15.94, -24) * mm, "radius": 3.25 * mm});
            skCircle(sketch, "E21.3.0", {"center": v(-23.9, -32.04) * mm, "radius": 3.25 * mm});
            skPoint(sketch, "E21.center", {"position": v(-15.9, -32) * mm});
            skCircle(sketch, "E22.0.1.0", {"center": v(-15.86, -8) * mm, "radius": 3.25 * mm});
            skCircle(sketch, "E22.0.1.1", {"center": v(-7.9, 0.04) * mm, "radius": 3.25 * mm});
            skCircle(sketch, "E22.0.1.2", {"center": v(-15.94, 8) * mm, "radius": 3.25 * mm});
            skCircle(sketch, "E22.0.1.3", {"center": v(-23.9, -0.04) * mm, "radius": 3.25 * mm});
            skCircle(sketch, "E22.0.2.0", {"center": v(-15.86, 24) * mm, "radius": 3.25 * mm});
            skCircle(sketch, "E22.0.2.1", {"center": v(-7.9, 32.04) * mm, "radius": 3.25 * mm});
            skCircle(sketch, "E22.0.2.2", {"center": v(-15.94, 40) * mm, "radius": 3.25 * mm});
            skCircle(sketch, "E22.0.2.3", {"center": v(-23.9, 31.96) * mm, "radius": 3.25 * mm});
            skLineSegment(sketch, "E22.direction1", {"start": v(-15.86, -40) * mm, "end": v(9.14, -40) * mm, "construction": true});
            skLineSegment(sketch, "E22.direction2", {"start": v(-15.86, -40) * mm, "end": v(-15.86, -8) * mm, "construction": true});
            skCircle(sketch, "E23", {"center": v(53.6, -8.35) * mm, "radius": 3 * mm});
            skCircle(sketch, "E24", {"center": v(53.6, 8.35) * mm, "radius": 3 * mm});
            skSolve(sketch);
        }
        {
            var Q0;
            Q0=makeQuery(id+"F16.imprint","IMPRINT",FACE,{"disambiguationData":[TD([[makeQuery(id+"F16.imprint","IMPRINT",EDGE,{"derivedFrom":sQuery(id+"F16.wireOp",EDGE,"E22.0.2.2")}),1.0]])]});
            var Q1;
            Q1=makeQuery(id+"F16.imprint","IMPRINT",FACE,{"disambiguationData":[TD([[makeQuery(id+"F16.imprint","IMPRINT",EDGE,{"derivedFrom":sQuery(id+"F16.wireOp",EDGE,"E22.0.2.3")}),1.0]])]});
            var Q2;
            Q2=makeQuery(id+"F16.imprint","IMPRINT",FACE,{"disambiguationData":[TD([[makeQuery(id+"F16.imprint","IMPRINT",EDGE,{"derivedFrom":sQuery(id+"F16.wireOp",EDGE,"E22.0.2.1")}),1.0]])]});
            var Q3;
            Q3=makeQuery(id+"F16.imprint","IMPRINT",FACE,{"disambiguationData":[TD([[makeQuery(id+"F16.imprint","IMPRINT",EDGE,{"derivedFrom":sQuery(id+"F16.wireOp",EDGE,"E22.0.2.0")}),1.0]])]});
            var Q4;
            Q4=makeQuery(id+"F16.imprint","IMPRINT",FACE,{"disambiguationData":[TD([[makeQuery(id+"F16.imprint","IMPRINT",EDGE,{"derivedFrom":sQuery(id+"F16.wireOp",EDGE,"E23")}),1.0]])]});
            var Q5;
            Q5=makeQuery(id+"F16.imprint","IMPRINT",FACE,{"disambiguationData":[TD([[makeQuery(id+"F16.imprint","IMPRINT",EDGE,{"derivedFrom":sQuery(id+"F16.wireOp",EDGE,"E22.0.1.2")}),1.0]])]});
            var Q6;
            Q6=makeQuery(id+"F16.imprint","IMPRINT",FACE,{"disambiguationData":[TD([[makeQuery(id+"F16.imprint","IMPRINT",EDGE,{"derivedFrom":sQuery(id+"F16.wireOp",EDGE,"E22.0.1.0")}),1.0]])]});
            var Q7;
            Q7=makeQuery(id+"F16.imprint","IMPRINT",FACE,{"disambiguationData":[TD([[makeQuery(id+"F16.imprint","IMPRINT",EDGE,{"derivedFrom":sQuery(id+"F16.wireOp",EDGE,"E21.2.0")}),1.0]])]});
            var Q8;
            Q8=makeQuery(id+"F16.imprint","IMPRINT",FACE,{"disambiguationData":[TD([[makeQuery(id+"F16.imprint","IMPRINT",EDGE,{"derivedFrom":sQuery(id+"F16.wireOp",EDGE,"E21.3.0")}),1.0]])]});
            var Q9;
            Q9=makeQuery(id+"F16.imprint","IMPRINT",FACE,{"disambiguationData":[TD([[makeQuery(id+"F16.imprint","IMPRINT",EDGE,{"derivedFrom":sQuery(id+"F16.wireOp",EDGE,"E21.1.0")}),1.0]])]});
            var Q10;
            Q10=makeQuery(id+"F16.imprint","IMPRINT",FACE,{"disambiguationData":[TD([[makeQuery(id+"F16.imprint","IMPRINT",EDGE,{"derivedFrom":sQuery(id+"F16.wireOp",EDGE,"E20")}),1.0]])]});
            var Q11;
            {var subQ0=sQuery(id+"F3.wireOp",EDGE,"E5.top");var subQ1=sQuery(id+"F3.wireOp",EDGE,"E5.bottom");var subQ2=sQuery(id+"F0.wireOp",EDGE,"E0.right");var subQ3=sQuery(id+"F0.wireOp",EDGE,"E0.top");var subQ4=sQuery(id+"F0.wireOp",EDGE,"E1.bottom");var subQ7=makeQuery(id+"F1.opRevolve","SWEPT_FACE",FACE,{"disambiguationData":[OSD([subQ4])]});Q11=makeQuery(id+"F16.imprint","IMPRINT",FACE,{"disambiguationData":[TD([[makeQuery(id+"F16.imprint","IMPRINT",EDGE,{"derivedFrom":makeQuery(id+"F9.boolean.opBoolean","INTERSECT",EDGE,{"derivedFrom":[makeQuery(id+"F8.boolean.opBoolean","MERGE",FACE,{"derivedFrom":[makeQuery(id+"F4.boolean.opBoolean","SPLIT",FACE,{"disambiguationData":[TD([makeQuery(id+"F4.opExtrude","SWEPT_FACE",FACE,{"disambiguationData":[OSD([subQ1])]})])],"derivedFrom":subQ7}),makeQuery(id+"F4.boolean.opBoolean","SPLIT",FACE,{"disambiguationData":[TD([makeQuery(id+"F4.opExtrude","SWEPT_FACE",FACE,{"disambiguationData":[OSD([subQ0])]})])],"derivedFrom":subQ7}),makeQuery(id+"F8.opExtrude","CAP_FACE",FACE,{"disambiguationData":[OSD([subQ3,subQ2,sQuery(id+"F6.wireOp",EDGE,"E7")])],"isStart":false}),makeQuery(id+"F8.opExtrude","CAP_FACE",FACE,{"disambiguationData":[OSD([subQ3,subQ2,sQuery(id+"F6.wireOp",EDGE,"E8")])],"isStart":false}),makeQuery(id+"F8.opExtrude","CAP_FACE",FACE,{"disambiguationData":[OSD([subQ1,subQ0,sQuery(id+"F6.wireOp",EDGE,"E9")])],"isStart":false}),makeQuery(id+"F8.opExtrude","CAP_FACE",FACE,{"disambiguationData":[OSD([subQ1,subQ0,sQuery(id+"F6.wireOp",EDGE,"E10")])],"isStart":false})]}),makeQuery(id+"F9.opExtrude","SWEPT_FACE",FACE,{"disambiguationData":[OSD([sQuery(id+"F7.wireOp",EDGE,"E14.0.2.2")])]})]})}),-1.0]])]});}
            var Q12;
            {var subQ0=sQuery(id+"F3.wireOp",EDGE,"E5.top");var subQ1=sQuery(id+"F3.wireOp",EDGE,"E5.bottom");var subQ2=sQuery(id+"F0.wireOp",EDGE,"E0.right");var subQ3=sQuery(id+"F0.wireOp",EDGE,"E0.top");var subQ4=sQuery(id+"F0.wireOp",EDGE,"E1.bottom");var subQ7=makeQuery(id+"F1.opRevolve","SWEPT_FACE",FACE,{"disambiguationData":[OSD([subQ4])]});Q12=makeQuery(id+"F16.imprint","IMPRINT",FACE,{"disambiguationData":[TD([[makeQuery(id+"F16.imprint","IMPRINT",EDGE,{"derivedFrom":makeQuery(id+"F9.boolean.opBoolean","INTERSECT",EDGE,{"derivedFrom":[makeQuery(id+"F8.boolean.opBoolean","MERGE",FACE,{"derivedFrom":[makeQuery(id+"F4.boolean.opBoolean","SPLIT",FACE,{"disambiguationData":[TD([makeQuery(id+"F4.opExtrude","SWEPT_FACE",FACE,{"disambiguationData":[OSD([subQ1])]})])],"derivedFrom":subQ7}),makeQuery(id+"F4.boolean.opBoolean","SPLIT",FACE,{"disambiguationData":[TD([makeQuery(id+"F4.opExtrude","SWEPT_FACE",FACE,{"disambiguationData":[OSD([subQ0])]})])],"derivedFrom":subQ7}),makeQuery(id+"F8.opExtrude","CAP_FACE",FACE,{"disambiguationData":[OSD([subQ3,subQ2,sQuery(id+"F6.wireOp",EDGE,"E7")])],"isStart":false}),makeQuery(id+"F8.opExtrude","CAP_FACE",FACE,{"disambiguationData":[OSD([subQ3,subQ2,sQuery(id+"F6.wireOp",EDGE,"E8")])],"isStart":false}),makeQuery(id+"F8.opExtrude","CAP_FACE",FACE,{"disambiguationData":[OSD([subQ1,subQ0,sQuery(id+"F6.wireOp",EDGE,"E9")])],"isStart":false}),makeQuery(id+"F8.opExtrude","CAP_FACE",FACE,{"disambiguationData":[OSD([subQ1,subQ0,sQuery(id+"F6.wireOp",EDGE,"E10")])],"isStart":false})]}),makeQuery(id+"F9.opExtrude","SWEPT_FACE",FACE,{"disambiguationData":[OSD([sQuery(id+"F7.wireOp",EDGE,"E14.0.2.4")])]})]})}),-1.0]])]});}
            var Q13;
            {var subQ0=sQuery(id+"F3.wireOp",EDGE,"E5.top");var subQ1=sQuery(id+"F3.wireOp",EDGE,"E5.bottom");var subQ2=sQuery(id+"F0.wireOp",EDGE,"E0.right");var subQ3=sQuery(id+"F0.wireOp",EDGE,"E0.top");var subQ4=sQuery(id+"F0.wireOp",EDGE,"E1.bottom");var subQ7=makeQuery(id+"F1.opRevolve","SWEPT_FACE",FACE,{"disambiguationData":[OSD([subQ4])]});Q13=makeQuery(id+"F16.imprint","IMPRINT",FACE,{"disambiguationData":[TD([[makeQuery(id+"F16.imprint","IMPRINT",EDGE,{"derivedFrom":makeQuery(id+"F9.boolean.opBoolean","INTERSECT",EDGE,{"derivedFrom":[makeQuery(id+"F8.boolean.opBoolean","MERGE",FACE,{"derivedFrom":[makeQuery(id+"F4.boolean.opBoolean","SPLIT",FACE,{"disambiguationData":[TD([makeQuery(id+"F4.opExtrude","SWEPT_FACE",FACE,{"disambiguationData":[OSD([subQ1])]})])],"derivedFrom":subQ7}),makeQuery(id+"F4.boolean.opBoolean","SPLIT",FACE,{"disambiguationData":[TD([makeQuery(id+"F4.opExtrude","SWEPT_FACE",FACE,{"disambiguationData":[OSD([subQ0])]})])],"derivedFrom":subQ7}),makeQuery(id+"F8.opExtrude","CAP_FACE",FACE,{"disambiguationData":[OSD([subQ3,subQ2,sQuery(id+"F6.wireOp",EDGE,"E7")])],"isStart":false}),makeQuery(id+"F8.opExtrude","CAP_FACE",FACE,{"disambiguationData":[OSD([subQ3,subQ2,sQuery(id+"F6.wireOp",EDGE,"E8")])],"isStart":false}),makeQuery(id+"F8.opExtrude","CAP_FACE",FACE,{"disambiguationData":[OSD([subQ1,subQ0,sQuery(id+"F6.wireOp",EDGE,"E9")])],"isStart":false}),makeQuery(id+"F8.opExtrude","CAP_FACE",FACE,{"disambiguationData":[OSD([subQ1,subQ0,sQuery(id+"F6.wireOp",EDGE,"E10")])],"isStart":false})]}),makeQuery(id+"F9.opExtrude","SWEPT_FACE",FACE,{"disambiguationData":[OSD([sQuery(id+"F7.wireOp",EDGE,"E14.0.2.6")])]})]})}),-1.0]])]});}
            var Q14;
            {var subQ0=sQuery(id+"F3.wireOp",EDGE,"E5.top");var subQ1=sQuery(id+"F3.wireOp",EDGE,"E5.bottom");var subQ2=sQuery(id+"F0.wireOp",EDGE,"E0.right");var subQ3=sQuery(id+"F0.wireOp",EDGE,"E0.top");var subQ4=sQuery(id+"F0.wireOp",EDGE,"E1.bottom");var subQ7=makeQuery(id+"F1.opRevolve","SWEPT_FACE",FACE,{"disambiguationData":[OSD([subQ4])]});Q14=makeQuery(id+"F16.imprint","IMPRINT",FACE,{"disambiguationData":[TD([[makeQuery(id+"F16.imprint","IMPRINT",EDGE,{"derivedFrom":makeQuery(id+"F9.boolean.opBoolean","INTERSECT",EDGE,{"derivedFrom":[makeQuery(id+"F8.boolean.opBoolean","MERGE",FACE,{"derivedFrom":[makeQuery(id+"F4.boolean.opBoolean","SPLIT",FACE,{"disambiguationData":[TD([makeQuery(id+"F4.opExtrude","SWEPT_FACE",FACE,{"disambiguationData":[OSD([subQ1])]})])],"derivedFrom":subQ7}),makeQuery(id+"F4.boolean.opBoolean","SPLIT",FACE,{"disambiguationData":[TD([makeQuery(id+"F4.opExtrude","SWEPT_FACE",FACE,{"disambiguationData":[OSD([subQ0])]})])],"derivedFrom":subQ7}),makeQuery(id+"F8.opExtrude","CAP_FACE",FACE,{"disambiguationData":[OSD([subQ3,subQ2,sQuery(id+"F6.wireOp",EDGE,"E7")])],"isStart":false}),makeQuery(id+"F8.opExtrude","CAP_FACE",FACE,{"disambiguationData":[OSD([subQ3,subQ2,sQuery(id+"F6.wireOp",EDGE,"E8")])],"isStart":false}),makeQuery(id+"F8.opExtrude","CAP_FACE",FACE,{"disambiguationData":[OSD([subQ1,subQ0,sQuery(id+"F6.wireOp",EDGE,"E9")])],"isStart":false}),makeQuery(id+"F8.opExtrude","CAP_FACE",FACE,{"disambiguationData":[OSD([subQ1,subQ0,sQuery(id+"F6.wireOp",EDGE,"E10")])],"isStart":false})]}),makeQuery(id+"F9.opExtrude","SWEPT_FACE",FACE,{"disambiguationData":[OSD([sQuery(id+"F7.wireOp",EDGE,"E14.0.2.0")])]})]})}),-1.0]])]});}
            var Q15;
            Q15=makeQuery(id+"F16.imprint","IMPRINT",FACE,{"disambiguationData":[TD([[makeQuery(id+"F16.imprint","IMPRINT",EDGE,{"derivedFrom":sQuery(id+"F16.wireOp",EDGE,"E24")}),1.0]])]});
            var Q16;
            {var subQ0=sQuery(id+"F3.wireOp",EDGE,"E5.top");var subQ1=sQuery(id+"F3.wireOp",EDGE,"E5.bottom");var subQ2=sQuery(id+"F0.wireOp",EDGE,"E0.right");var subQ3=sQuery(id+"F0.wireOp",EDGE,"E0.top");var subQ4=sQuery(id+"F0.wireOp",EDGE,"E1.bottom");var subQ7=makeQuery(id+"F1.opRevolve","SWEPT_FACE",FACE,{"disambiguationData":[OSD([subQ4])]});Q16=makeQuery(id+"F16.imprint","IMPRINT",FACE,{"disambiguationData":[TD([[makeQuery(id+"F16.imprint","IMPRINT",EDGE,{"derivedFrom":makeQuery(id+"F9.boolean.opBoolean","INTERSECT",EDGE,{"derivedFrom":[makeQuery(id+"F8.boolean.opBoolean","MERGE",FACE,{"derivedFrom":[makeQuery(id+"F4.boolean.opBoolean","SPLIT",FACE,{"disambiguationData":[TD([makeQuery(id+"F4.opExtrude","SWEPT_FACE",FACE,{"disambiguationData":[OSD([subQ1])]})])],"derivedFrom":subQ7}),makeQuery(id+"F4.boolean.opBoolean","SPLIT",FACE,{"disambiguationData":[TD([makeQuery(id+"F4.opExtrude","SWEPT_FACE",FACE,{"disambiguationData":[OSD([subQ0])]})])],"derivedFrom":subQ7}),makeQuery(id+"F8.opExtrude","CAP_FACE",FACE,{"disambiguationData":[OSD([subQ3,subQ2,sQuery(id+"F6.wireOp",EDGE,"E7")])],"isStart":false}),makeQuery(id+"F8.opExtrude","CAP_FACE",FACE,{"disambiguationData":[OSD([subQ3,subQ2,sQuery(id+"F6.wireOp",EDGE,"E8")])],"isStart":false}),makeQuery(id+"F8.opExtrude","CAP_FACE",FACE,{"disambiguationData":[OSD([subQ1,subQ0,sQuery(id+"F6.wireOp",EDGE,"E9")])],"isStart":false}),makeQuery(id+"F8.opExtrude","CAP_FACE",FACE,{"disambiguationData":[OSD([subQ1,subQ0,sQuery(id+"F6.wireOp",EDGE,"E10")])],"isStart":false})]}),makeQuery(id+"F9.opExtrude","SWEPT_FACE",FACE,{"disambiguationData":[OSD([sQuery(id+"F7.wireOp",EDGE,"E14.0.1.4")])]})]})}),-1.0]])]});}
            var Q17;
            {var subQ0=sQuery(id+"F3.wireOp",EDGE,"E5.top");var subQ1=sQuery(id+"F3.wireOp",EDGE,"E5.bottom");var subQ2=sQuery(id+"F0.wireOp",EDGE,"E0.right");var subQ3=sQuery(id+"F0.wireOp",EDGE,"E0.top");var subQ4=sQuery(id+"F0.wireOp",EDGE,"E1.bottom");var subQ7=makeQuery(id+"F1.opRevolve","SWEPT_FACE",FACE,{"disambiguationData":[OSD([subQ4])]});Q17=makeQuery(id+"F16.imprint","IMPRINT",FACE,{"disambiguationData":[TD([[makeQuery(id+"F16.imprint","IMPRINT",EDGE,{"derivedFrom":makeQuery(id+"F9.boolean.opBoolean","INTERSECT",EDGE,{"derivedFrom":[makeQuery(id+"F8.boolean.opBoolean","MERGE",FACE,{"derivedFrom":[makeQuery(id+"F4.boolean.opBoolean","SPLIT",FACE,{"disambiguationData":[TD([makeQuery(id+"F4.opExtrude","SWEPT_FACE",FACE,{"disambiguationData":[OSD([subQ1])]})])],"derivedFrom":subQ7}),makeQuery(id+"F4.boolean.opBoolean","SPLIT",FACE,{"disambiguationData":[TD([makeQuery(id+"F4.opExtrude","SWEPT_FACE",FACE,{"disambiguationData":[OSD([subQ0])]})])],"derivedFrom":subQ7}),makeQuery(id+"F8.opExtrude","CAP_FACE",FACE,{"disambiguationData":[OSD([subQ3,subQ2,sQuery(id+"F6.wireOp",EDGE,"E7")])],"isStart":false}),makeQuery(id+"F8.opExtrude","CAP_FACE",FACE,{"disambiguationData":[OSD([subQ3,subQ2,sQuery(id+"F6.wireOp",EDGE,"E8")])],"isStart":false}),makeQuery(id+"F8.opExtrude","CAP_FACE",FACE,{"disambiguationData":[OSD([subQ1,subQ0,sQuery(id+"F6.wireOp",EDGE,"E9")])],"isStart":false}),makeQuery(id+"F8.opExtrude","CAP_FACE",FACE,{"disambiguationData":[OSD([subQ1,subQ0,sQuery(id+"F6.wireOp",EDGE,"E10")])],"isStart":false})]}),makeQuery(id+"F9.opExtrude","SWEPT_FACE",FACE,{"disambiguationData":[OSD([sQuery(id+"F7.wireOp",EDGE,"E14.0.1.0")])]})]})}),-1.0]])]});}
            var Q18;
            {var subQ0=sQuery(id+"F3.wireOp",EDGE,"E5.top");var subQ1=sQuery(id+"F3.wireOp",EDGE,"E5.bottom");var subQ2=sQuery(id+"F0.wireOp",EDGE,"E0.right");var subQ3=sQuery(id+"F0.wireOp",EDGE,"E0.top");var subQ4=sQuery(id+"F0.wireOp",EDGE,"E1.bottom");var subQ7=makeQuery(id+"F1.opRevolve","SWEPT_FACE",FACE,{"disambiguationData":[OSD([subQ4])]});Q18=makeQuery(id+"F16.imprint","IMPRINT",FACE,{"disambiguationData":[TD([[makeQuery(id+"F16.imprint","IMPRINT",EDGE,{"derivedFrom":makeQuery(id+"F9.boolean.opBoolean","INTERSECT",EDGE,{"derivedFrom":[makeQuery(id+"F8.boolean.opBoolean","MERGE",FACE,{"derivedFrom":[makeQuery(id+"F4.boolean.opBoolean","SPLIT",FACE,{"disambiguationData":[TD([makeQuery(id+"F4.opExtrude","SWEPT_FACE",FACE,{"disambiguationData":[OSD([subQ1])]})])],"derivedFrom":subQ7}),makeQuery(id+"F4.boolean.opBoolean","SPLIT",FACE,{"disambiguationData":[TD([makeQuery(id+"F4.opExtrude","SWEPT_FACE",FACE,{"disambiguationData":[OSD([subQ0])]})])],"derivedFrom":subQ7}),makeQuery(id+"F8.opExtrude","CAP_FACE",FACE,{"disambiguationData":[OSD([subQ3,subQ2,sQuery(id+"F6.wireOp",EDGE,"E7")])],"isStart":false}),makeQuery(id+"F8.opExtrude","CAP_FACE",FACE,{"disambiguationData":[OSD([subQ3,subQ2,sQuery(id+"F6.wireOp",EDGE,"E8")])],"isStart":false}),makeQuery(id+"F8.opExtrude","CAP_FACE",FACE,{"disambiguationData":[OSD([subQ1,subQ0,sQuery(id+"F6.wireOp",EDGE,"E9")])],"isStart":false}),makeQuery(id+"F8.opExtrude","CAP_FACE",FACE,{"disambiguationData":[OSD([subQ1,subQ0,sQuery(id+"F6.wireOp",EDGE,"E10")])],"isStart":false})]}),makeQuery(id+"F9.opExtrude","SWEPT_FACE",FACE,{"disambiguationData":[OSD([sQuery(id+"F7.wireOp",EDGE,"E13.4.0")])]})]})}),-1.0]])]});}
            var Q19;
            {var subQ0=sQuery(id+"F3.wireOp",EDGE,"E5.top");var subQ1=sQuery(id+"F3.wireOp",EDGE,"E5.bottom");var subQ2=sQuery(id+"F0.wireOp",EDGE,"E0.right");var subQ3=sQuery(id+"F0.wireOp",EDGE,"E0.top");var subQ4=sQuery(id+"F0.wireOp",EDGE,"E1.bottom");var subQ7=makeQuery(id+"F1.opRevolve","SWEPT_FACE",FACE,{"disambiguationData":[OSD([subQ4])]});Q19=makeQuery(id+"F16.imprint","IMPRINT",FACE,{"disambiguationData":[TD([[makeQuery(id+"F16.imprint","IMPRINT",EDGE,{"derivedFrom":makeQuery(id+"F9.boolean.opBoolean","INTERSECT",EDGE,{"derivedFrom":[makeQuery(id+"F8.boolean.opBoolean","MERGE",FACE,{"derivedFrom":[makeQuery(id+"F4.boolean.opBoolean","SPLIT",FACE,{"disambiguationData":[TD([makeQuery(id+"F4.opExtrude","SWEPT_FACE",FACE,{"disambiguationData":[OSD([subQ1])]})])],"derivedFrom":subQ7}),makeQuery(id+"F4.boolean.opBoolean","SPLIT",FACE,{"disambiguationData":[TD([makeQuery(id+"F4.opExtrude","SWEPT_FACE",FACE,{"disambiguationData":[OSD([subQ0])]})])],"derivedFrom":subQ7}),makeQuery(id+"F8.opExtrude","CAP_FACE",FACE,{"disambiguationData":[OSD([subQ3,subQ2,sQuery(id+"F6.wireOp",EDGE,"E7")])],"isStart":false}),makeQuery(id+"F8.opExtrude","CAP_FACE",FACE,{"disambiguationData":[OSD([subQ3,subQ2,sQuery(id+"F6.wireOp",EDGE,"E8")])],"isStart":false}),makeQuery(id+"F8.opExtrude","CAP_FACE",FACE,{"disambiguationData":[OSD([subQ1,subQ0,sQuery(id+"F6.wireOp",EDGE,"E9")])],"isStart":false}),makeQuery(id+"F8.opExtrude","CAP_FACE",FACE,{"disambiguationData":[OSD([subQ1,subQ0,sQuery(id+"F6.wireOp",EDGE,"E10")])],"isStart":false})]}),makeQuery(id+"F9.opExtrude","SWEPT_FACE",FACE,{"disambiguationData":[OSD([sQuery(id+"F7.wireOp",EDGE,"E13.6.0")])]})]})}),-1.0]])]});}
            var Q20;
            {var subQ0=sQuery(id+"F3.wireOp",EDGE,"E5.top");var subQ1=sQuery(id+"F3.wireOp",EDGE,"E5.bottom");var subQ2=sQuery(id+"F0.wireOp",EDGE,"E0.right");var subQ3=sQuery(id+"F0.wireOp",EDGE,"E0.top");var subQ4=sQuery(id+"F0.wireOp",EDGE,"E1.bottom");var subQ7=makeQuery(id+"F1.opRevolve","SWEPT_FACE",FACE,{"disambiguationData":[OSD([subQ4])]});Q20=makeQuery(id+"F16.imprint","IMPRINT",FACE,{"disambiguationData":[TD([[makeQuery(id+"F16.imprint","IMPRINT",EDGE,{"derivedFrom":makeQuery(id+"F9.boolean.opBoolean","INTERSECT",EDGE,{"derivedFrom":[makeQuery(id+"F8.boolean.opBoolean","MERGE",FACE,{"derivedFrom":[makeQuery(id+"F4.boolean.opBoolean","SPLIT",FACE,{"disambiguationData":[TD([makeQuery(id+"F4.opExtrude","SWEPT_FACE",FACE,{"disambiguationData":[OSD([subQ1])]})])],"derivedFrom":subQ7}),makeQuery(id+"F4.boolean.opBoolean","SPLIT",FACE,{"disambiguationData":[TD([makeQuery(id+"F4.opExtrude","SWEPT_FACE",FACE,{"disambiguationData":[OSD([subQ0])]})])],"derivedFrom":subQ7}),makeQuery(id+"F8.opExtrude","CAP_FACE",FACE,{"disambiguationData":[OSD([subQ3,subQ2,sQuery(id+"F6.wireOp",EDGE,"E7")])],"isStart":false}),makeQuery(id+"F8.opExtrude","CAP_FACE",FACE,{"disambiguationData":[OSD([subQ3,subQ2,sQuery(id+"F6.wireOp",EDGE,"E8")])],"isStart":false}),makeQuery(id+"F8.opExtrude","CAP_FACE",FACE,{"disambiguationData":[OSD([subQ1,subQ0,sQuery(id+"F6.wireOp",EDGE,"E9")])],"isStart":false}),makeQuery(id+"F8.opExtrude","CAP_FACE",FACE,{"disambiguationData":[OSD([subQ1,subQ0,sQuery(id+"F6.wireOp",EDGE,"E10")])],"isStart":false})]}),makeQuery(id+"F9.opExtrude","SWEPT_FACE",FACE,{"disambiguationData":[OSD([sQuery(id+"F7.wireOp",EDGE,"E12")])]})]})}),-1.0]])]});}
            var Q21;
            {var subQ0=sQuery(id+"F3.wireOp",EDGE,"E5.top");var subQ1=sQuery(id+"F3.wireOp",EDGE,"E5.bottom");var subQ2=sQuery(id+"F0.wireOp",EDGE,"E0.right");var subQ3=sQuery(id+"F0.wireOp",EDGE,"E0.top");var subQ4=sQuery(id+"F0.wireOp",EDGE,"E1.bottom");var subQ7=makeQuery(id+"F1.opRevolve","SWEPT_FACE",FACE,{"disambiguationData":[OSD([subQ4])]});Q21=makeQuery(id+"F16.imprint","IMPRINT",FACE,{"disambiguationData":[TD([[makeQuery(id+"F16.imprint","IMPRINT",EDGE,{"derivedFrom":makeQuery(id+"F9.boolean.opBoolean","INTERSECT",EDGE,{"derivedFrom":[makeQuery(id+"F8.boolean.opBoolean","MERGE",FACE,{"derivedFrom":[makeQuery(id+"F4.boolean.opBoolean","SPLIT",FACE,{"disambiguationData":[TD([makeQuery(id+"F4.opExtrude","SWEPT_FACE",FACE,{"disambiguationData":[OSD([subQ1])]})])],"derivedFrom":subQ7}),makeQuery(id+"F4.boolean.opBoolean","SPLIT",FACE,{"disambiguationData":[TD([makeQuery(id+"F4.opExtrude","SWEPT_FACE",FACE,{"disambiguationData":[OSD([subQ0])]})])],"derivedFrom":subQ7}),makeQuery(id+"F8.opExtrude","CAP_FACE",FACE,{"disambiguationData":[OSD([subQ3,subQ2,sQuery(id+"F6.wireOp",EDGE,"E7")])],"isStart":false}),makeQuery(id+"F8.opExtrude","CAP_FACE",FACE,{"disambiguationData":[OSD([subQ3,subQ2,sQuery(id+"F6.wireOp",EDGE,"E8")])],"isStart":false}),makeQuery(id+"F8.opExtrude","CAP_FACE",FACE,{"disambiguationData":[OSD([subQ1,subQ0,sQuery(id+"F6.wireOp",EDGE,"E9")])],"isStart":false}),makeQuery(id+"F8.opExtrude","CAP_FACE",FACE,{"disambiguationData":[OSD([subQ1,subQ0,sQuery(id+"F6.wireOp",EDGE,"E10")])],"isStart":false})]}),makeQuery(id+"F9.opExtrude","SWEPT_FACE",FACE,{"disambiguationData":[OSD([sQuery(id+"F7.wireOp",EDGE,"E13.2.0")])]})]})}),-1.0]])]});}
            extrude(context, id + "F17", {"entities" : qUnion([Q0, Q1, Q2, Q3, Q4, Q5, Q6, Q7, Q8, Q9, Q10, Q11, Q12, Q13, Q14, Q15, Q16, Q17, Q18, Q19, Q20, Q21]), "depth" : 6 * mm, "offsetDistance" : 25 * mm, "hasSecondDirection" : true, "secondDirectionOppositeDirection" : false, "secondDirectionDepth" : .25 * mm});
        }
        {
            var Q0;
            Q0=qCreatedBy(makeId("Top.planeOp"),FACE);
            var sketch = newSketch(context, id + "F18", { "sketchPlane" : qUnion([Q0])});
            skLineSegment(sketch, "E25.bottom", {"start": v(-46.3, 0.05) * mm, "end": v(93.7, 0.05) * mm});
            skLineSegment(sketch, "E25.top", {"start": v(-46.3, -0.05) * mm, "end": v(93.7, -0.05) * mm});
            skLineSegment(sketch, "E25.left", {"start": v(-46.3, 0.05) * mm, "end": v(-46.3, -0.05) * mm});
            skLineSegment(sketch, "E25.right", {"start": v(93.7, 0.05) * mm, "end": v(93.7, -0.05) * mm});
            skSolve(sketch);
        }
        {
            var Q0;
            {var subQ0=sQuery(id+"F18.wireOp",EDGE,"E25.left");Q0=makeQuery(id+"F18.imprint","IMPRINT",FACE,{"disambiguationData":[TD([[makeQuery(id+"F18.imprint","IMPRINT",EDGE,{"derivedFrom":subQ0}),1.0]])]});}
            extrude(context, id + "F19", {"entities" : qUnion([Q0]), "operationType" : NewBodyOperationType.REMOVE, "endBound" : BoundingType.THROUGH_ALL, "oppositeDirection" : true, "depth" : 25 * mm, "offsetDistance" : 25 * mm, "hasSecondDirection" : true, "secondDirectionBound" : SecondDirectionBoundingType.THROUGH_ALL, "secondDirectionOppositeDirection" : false, "secondDirectionDepth" : 25 * mm});
        }
        {
            var Q0;
            {var subQ0=sQuery(id+"F10.wireOp",EDGE,"E15.left");var subQ1=sQuery(id+"F3.wireOp",EDGE,"E6.1.0");var subQ3=sQuery(id+"F3.wireOp",EDGE,"E5.top");var subQ4=makeQuery(id+"F4.opExtrude","SWEPT_FACE",FACE,{"disambiguationData":[OSD([subQ3])]});var subQ6=sQuery(id+"F0.wireOp",EDGE,"E0.right");var subQ7=sQuery(id+"F0.wireOp",EDGE,"E0.top");var subQ9=sQuery(id+"F0.wireOp",EDGE,"E2.right");var subQ12=sQuery(id+"F3.wireOp",EDGE,"E5.bottom");var subQ16=sQuery(id+"F0.wireOp",EDGE,"E1.bottom");var subQ28=sQuery(id+"F10.wireOp",EDGE,"E15.right");var subQ32=sQuery(id+"F0.wireOp",EDGE,"E1.left");var subQ38=sQuery(id+"F0.wireOp",EDGE,"E2.top");var subQ39=makeQuery(id+"F1.opRevolve","SWEPT_FACE",FACE,{"disambiguationData":[OSD([subQ38])]});var subQ40=sQuery(id+"F3.wireOp",EDGE,"E6.11.1");var subQ41=makeQuery(id+"F4.opExtrude","CAP_FACE",FACE,{"disambiguationData":[OSD([subQ6,subQ16,subQ32,subQ9,subQ40])],"isStart":false});var subQ42=makeQuery(id+"F1.opRevolve","SWEPT_FACE",FACE,{"disambiguationData":[OSD([subQ7])]});var subQ43=makeQuery(id+"F4.opExtrude","CAP_FACE",FACE,{"disambiguationData":[OSD([subQ12,subQ3,sQuery(id+"F3.wireOp",EDGE,"E5.left"),sQuery(id+"F3.wireOp",EDGE,"E5.right")])],"isStart":false});var subQ44=makeQuery(id+"F4.opExtrude","CAP_FACE",FACE,{"disambiguationData":[OSD([subQ6,subQ16,subQ32,subQ9,subQ1])],"isStart":false});var subQ45=makeQuery(id+"F11.opExtrude","CAP_FACE",FACE,{"disambiguationData":[OSD([subQ12,subQ40,subQ0,subQ28])],"isStart":false});var subQ46=makeQuery(id+"F11.opExtrude","CAP_FACE",FACE,{"disambiguationData":[OSD([subQ3,subQ1,subQ0,subQ28])],"isStart":false});var subQ52=sQuery(id+"F0.wireOp",EDGE,"E0.left");var subQ53=makeQuery(id+"F1.opRevolve","SWEPT_FACE",FACE,{"disambiguationData":[OSD([subQ52])]});Q0=makeQuery(id+"F19.boolean.opBoolean","SPLIT",FACE,{"disambiguationData":[TD([subQ4])],"derivedFrom":makeQuery(id+"F13.boolean.opBoolean","SPLIT",FACE,{"disambiguationData":[TD([subQ53])],"derivedFrom":makeQuery(id+"F11.boolean.opBoolean","MERGE",FACE,{"derivedFrom":[makeQuery(id+"F8.boolean.opBoolean","SPLIT",FACE,{"disambiguationData":[TD([subQ53])],"derivedFrom":makeQuery(id+"F4.boolean.opBoolean","MERGE",FACE,{"derivedFrom":[subQ42,subQ39,subQ43,subQ44,subQ41]})}),subQ45,subQ46]})})});}
            var sketch = newSketch(context, id + "F20", { "sketchPlane" : qUnion([Q0])});
            skLineSegment(sketch, "E26.bottom", {"start": v(0.14, -48) * mm, "end": v(-15.86, -48) * mm});
            skLineSegment(sketch, "E26.top", {"start": v(0.14, 0) * mm, "end": v(-31.86, 0) * mm});
            skLineSegment(sketch, "E26.left", {"start": v(0.14, -48) * mm, "end": v(0.14, 0) * mm});
            skLineSegment(sketch, "E26.right", {"start": v(-31.86, -32) * mm, "end": v(-31.86, 0) * mm});
            skPoint(sketch, "E27.visualSharp", {"position": v(-31.86, -48) * mm});
            skArc(sketch, "E27.filletArc", {"start": v(-31.86, -32) * mm, "mid": v(-27.17, -43.31) * mm, "end": v(-15.86, -48) * mm});
            skSolve(sketch);
        }
        {
            var Q0;
            {var subQ0=sQuery(id+"F10.wireOp",EDGE,"E15.left");var subQ1=sQuery(id+"F3.wireOp",EDGE,"E6.11.1");var subQ4=sQuery(id+"F0.wireOp",EDGE,"E0.right");var subQ5=sQuery(id+"F0.wireOp",EDGE,"E0.top");var subQ7=sQuery(id+"F0.wireOp",EDGE,"E2.right");var subQ10=sQuery(id+"F3.wireOp",EDGE,"E5.bottom");var subQ12=sQuery(id+"F3.wireOp",EDGE,"E5.top");var subQ15=makeQuery(id+"F4.opExtrude","SWEPT_FACE",FACE,{"disambiguationData":[OSD([subQ10])]});var subQ17=sQuery(id+"F0.wireOp",EDGE,"E1.bottom");var subQ32=sQuery(id+"F0.wireOp",EDGE,"E2.top");var subQ35=sQuery(id+"F0.wireOp",EDGE,"E0.left");var subQ41=makeQuery(id+"F1.opRevolve","SWEPT_FACE",FACE,{"disambiguationData":[OSD([subQ32])]});var subQ42=sQuery(id+"F0.wireOp",EDGE,"E1.left");var subQ43=makeQuery(id+"F4.opExtrude","CAP_FACE",FACE,{"disambiguationData":[OSD([subQ4,subQ17,subQ42,subQ7,subQ1])],"isStart":false});var subQ44=makeQuery(id+"F1.opRevolve","SWEPT_FACE",FACE,{"disambiguationData":[OSD([subQ5])]});var subQ45=makeQuery(id+"F4.opExtrude","CAP_FACE",FACE,{"disambiguationData":[OSD([subQ10,subQ12,sQuery(id+"F3.wireOp",EDGE,"E5.left"),sQuery(id+"F3.wireOp",EDGE,"E5.right")])],"isStart":false});var subQ46=sQuery(id+"F3.wireOp",EDGE,"E6.1.0");var subQ47=makeQuery(id+"F4.opExtrude","CAP_FACE",FACE,{"disambiguationData":[OSD([subQ4,subQ17,subQ42,subQ7,subQ46])],"isStart":false});var subQ48=sQuery(id+"F10.wireOp",EDGE,"E15.right");var subQ49=makeQuery(id+"F11.opExtrude","CAP_FACE",FACE,{"disambiguationData":[OSD([subQ10,subQ1,subQ0,subQ48])],"isStart":false});var subQ50=makeQuery(id+"F11.opExtrude","CAP_FACE",FACE,{"disambiguationData":[OSD([subQ12,subQ46,subQ0,subQ48])],"isStart":false});var subQ57=makeQuery(id+"F1.opRevolve","SWEPT_FACE",FACE,{"disambiguationData":[OSD([subQ35])]});Q0=makeQuery(id+"F19.boolean.opBoolean","SPLIT",FACE,{"disambiguationData":[TD([subQ15])],"derivedFrom":makeQuery(id+"F13.boolean.opBoolean","SPLIT",FACE,{"disambiguationData":[TD([subQ57])],"derivedFrom":makeQuery(id+"F11.boolean.opBoolean","MERGE",FACE,{"derivedFrom":[makeQuery(id+"F8.boolean.opBoolean","SPLIT",FACE,{"disambiguationData":[TD([subQ57])],"derivedFrom":makeQuery(id+"F4.boolean.opBoolean","MERGE",FACE,{"derivedFrom":[subQ44,subQ41,subQ45,subQ47,subQ43]})}),subQ49,subQ50]})})});}
            var sketch = newSketch(context, id + "F21", { "sketchPlane" : qUnion([Q0])});
            skLineSegment(sketch, "E28.bottom", {"start": v(-15.86, 48) * mm, "end": v(0.14, 48) * mm});
            skLineSegment(sketch, "E28.top", {"start": v(-31.86, 0) * mm, "end": v(0.14, 0) * mm});
            skLineSegment(sketch, "E28.left", {"start": v(-31.86, 32) * mm, "end": v(-31.86, 0) * mm});
            skLineSegment(sketch, "E28.right", {"start": v(0.14, 48) * mm, "end": v(0.14, 0) * mm});
            skPoint(sketch, "E29.visualSharp", {"position": v(-31.86, 48) * mm});
            skArc(sketch, "E29.filletArc", {"start": v(-15.86, 48) * mm, "mid": v(-27.17, 43.31) * mm, "end": v(-31.86, 32) * mm});
            skSolve(sketch);
        }
        {
            var Q0;
            {var subQ0=sQuery(id+"F6.wireOp",EDGE,"E8");var subQ1=makeQuery(id+"F8.boolean.opBoolean","COPY",EDGE,{"derivedFrom":makeQuery(id+"F8.opExtrude","CAP_EDGE",EDGE,{"disambiguationData":[OSD([subQ0])],"isStart":true})});Q0=makeQuery(id+"F20.imprint","IMPRINT",FACE,{"disambiguationData":[TD([[makeQuery(id+"F20.imprint","IMPRINT",EDGE,{"derivedFrom":subQ1}),-1.0]])]});}
            var Q1;
            {var subQ81=sQuery(id+"F20.wireOp",EDGE,"E26.top");Q1=makeQuery(id+"F20.imprint","IMPRINT",FACE,{"disambiguationData":[TD([[makeQuery(id+"F20.imprint","IMPRINT",EDGE,{"derivedFrom":subQ81}),1.0]])]});}
            var Q2;
            {var subQ12=sQuery(id+"F3.wireOp",EDGE,"E5.top");var subQ13=sQuery(id+"F3.wireOp",EDGE,"E5.bottom");var subQ29=makeQuery(id+"F4.opExtrude","SWEPT_FACE",FACE,{"disambiguationData":[OSD([subQ12])]});var subQ31=sQuery(id+"F6.wireOp",EDGE,"E10");var subQ32=makeQuery(id+"F4.opExtrude","CAP_EDGE",EDGE,{"disambiguationData":[OSD([subQ13])],"isStart":false});var subQ34=makeQuery(id+"F6.imprint","IMPRINT",EDGE,{"disambiguationData":[TD([[makeQuery(id+"F6.imprint","INTERSECT",VERTEX,{"disambiguationData":[OD(1.0)],"derivedFrom":[subQ32,subQ31]}),1.0]])],"derivedFrom":subQ31});var subQ69=makeQuery(id+"F19.boolean.opBoolean","SPLIT",EDGE,{"disambiguationData":[TD([subQ29])],"derivedFrom":makeQuery(id+"F8.boolean.opBoolean","COPY",EDGE,{"derivedFrom":makeQuery(id+"F8.opExtrude","CAP_EDGE",EDGE,{"disambiguationData":[OSD([subQ31]),TDD([subQ34])],"isStart":true})})});Q2=makeQuery(id+"F20.imprint","IMPRINT",FACE,{"disambiguationData":[TD([[makeQuery(id+"F20.imprint","IMPRINT",EDGE,{"derivedFrom":subQ69}),-1.0]])]});}
            var Q3;
            {var subQ22=sQuery(id+"F6.wireOp",EDGE,"E7");var subQ23=makeQuery(id+"F8.boolean.opBoolean","COPY",EDGE,{"derivedFrom":makeQuery(id+"F8.opExtrude","CAP_EDGE",EDGE,{"disambiguationData":[OSD([subQ22])],"isStart":true})});Q3=makeQuery(id+"F21.imprint","IMPRINT",FACE,{"disambiguationData":[TD([[makeQuery(id+"F21.imprint","IMPRINT",EDGE,{"derivedFrom":subQ23}),-1.0]])]});}
            var Q4;
            {var subQ79=sQuery(id+"F21.wireOp",EDGE,"E28.top");Q4=makeQuery(id+"F21.imprint","IMPRINT",FACE,{"disambiguationData":[TD([[makeQuery(id+"F21.imprint","IMPRINT",EDGE,{"derivedFrom":subQ79}),1.0]])]});}
            var Q5;
            {var subQ13=sQuery(id+"F3.wireOp",EDGE,"E5.bottom");var subQ31=sQuery(id+"F6.wireOp",EDGE,"E10");var subQ32=makeQuery(id+"F4.opExtrude","CAP_EDGE",EDGE,{"disambiguationData":[OSD([subQ13])],"isStart":false});var subQ34=makeQuery(id+"F6.imprint","IMPRINT",EDGE,{"disambiguationData":[TD([[makeQuery(id+"F6.imprint","INTERSECT",VERTEX,{"disambiguationData":[OD(1.0)],"derivedFrom":[subQ32,subQ31]}),1.0]])],"derivedFrom":subQ31});var subQ47=makeQuery(id+"F4.opExtrude","SWEPT_FACE",FACE,{"disambiguationData":[OSD([subQ13])]});var subQ69=makeQuery(id+"F19.boolean.opBoolean","SPLIT",EDGE,{"disambiguationData":[TD([subQ47])],"derivedFrom":makeQuery(id+"F8.boolean.opBoolean","COPY",EDGE,{"derivedFrom":makeQuery(id+"F8.opExtrude","CAP_EDGE",EDGE,{"disambiguationData":[OSD([subQ31]),TDD([subQ34])],"isStart":true})})});Q5=makeQuery(id+"F21.imprint","IMPRINT",FACE,{"disambiguationData":[TD([[makeQuery(id+"F21.imprint","IMPRINT",EDGE,{"derivedFrom":subQ69}),-1.0]])]});}
            var Q6;
            {var subQ2=sQuery(id+"F0.wireOp",EDGE,"E0.right");var subQ3=sQuery(id+"F0.wireOp",EDGE,"E0.top");var subQ4=sQuery(id+"F0.wireOp",EDGE,"E1.bottom");var subQ6=sQuery(id+"F6.wireOp",EDGE,"E10");var subQ7=sQuery(id+"F3.wireOp",EDGE,"E5.bottom");var subQ9=sQuery(id+"F3.wireOp",EDGE,"E5.top");var subQ13=sQuery(id+"F6.wireOp",EDGE,"E9");var subQ19=sQuery(id+"F6.wireOp",EDGE,"E8");var subQ22=makeQuery(id+"F4.opExtrude","SWEPT_FACE",FACE,{"disambiguationData":[OSD([subQ9])]});var subQ23=sQuery(id+"F6.wireOp",EDGE,"E7");var subQ24=makeQuery(id+"F8.opExtrude","CAP_FACE",FACE,{"disambiguationData":[OSD([subQ3,subQ2,subQ23])],"isStart":false});var subQ26=makeQuery(id+"F1.opRevolve","SWEPT_FACE",FACE,{"disambiguationData":[OSD([subQ4])]});var subQ27=makeQuery(id+"F8.opExtrude","CAP_FACE",FACE,{"disambiguationData":[OSD([subQ3,subQ2,subQ19])],"isStart":false});var subQ28=makeQuery(id+"F8.opExtrude","CAP_FACE",FACE,{"disambiguationData":[OSD([subQ7,subQ9,subQ13])],"isStart":false});var subQ29=makeQuery(id+"F8.opExtrude","CAP_FACE",FACE,{"disambiguationData":[OSD([subQ7,subQ9,subQ6])],"isStart":false});var subQ35=makeQuery(id+"F4.opExtrude","SWEPT_FACE",FACE,{"disambiguationData":[OSD([subQ7])]});Q6=makeQuery(id+"F19.boolean.opBoolean","SPLIT",FACE,{"disambiguationData":[TD([subQ22])],"derivedFrom":makeQuery(id+"F11.boolean.opBoolean","SPLIT",FACE,{"disambiguationData":[TD([makeQuery(id+"F8.boolean.opBoolean","COPY",FACE,{"derivedFrom":makeQuery(id+"F8.opExtrude","SWEPT_FACE",FACE,{"disambiguationData":[OSD([subQ23])]})})])],"derivedFrom":makeQuery(id+"F8.boolean.opBoolean","MERGE",FACE,{"derivedFrom":[makeQuery(id+"F4.boolean.opBoolean","SPLIT",FACE,{"disambiguationData":[TD([subQ35])],"derivedFrom":subQ26}),makeQuery(id+"F4.boolean.opBoolean","SPLIT",FACE,{"disambiguationData":[TD([subQ22])],"derivedFrom":subQ26}),subQ24,subQ27,subQ28,subQ29]})})});}
            extrude(context, id + "F22", {"entities" : qUnion([Q0, Q1, Q2, Q3, Q4, Q5]), "operationType" : NewBodyOperationType.REMOVE, "endBound" : BoundingType.UP_TO_SURFACE, "oppositeDirection" : true, "depth" : 25 * mm, "endBoundEntityFace" : qUnion([Q6]), "offsetDistance" : 25 * mm});
        }
    });
